# Revit family: 540_Sliding_Window_XXXX_Standard
name_source: partatom
category: Windows
revit_build: Autodesk Revit 2014 (Build: 20130308_1515(x64)
units: mm (PartAtom-declared; Revit-internal decimal feet)

## types (81) — shared parameters
Astragal Sash Gap = 1 mm  [stored 0.00328084 ft]
Centered In Wall = Yes
Custom Sash Width Side = 1000 mm  [stored 3.28084 ft]
Default Sill Height = 800 mm
Description = Sliding window, XXXX
Equal Sash Width = Yes
Frame Thickness = 54 mm  [stored 0.177165 ft]
Heavy Duty Handle Gap = 27 mm
Limit Sash Height Max = 1500 mm  [stored 4.92126 ft]
Limit Sash Height Min = 300 mm  [stored 0.984252 ft]
Limit Sash Width Max = 1200 mm
Limit Sash Width Min = 300 mm  [stored 0.984252 ft]
Limit Window Height Max = 1580 mm
Limit Window Height Min = 380 mm
Limit Window Width Max = 4760 mm
Limit Window Width Min = 1160 mm
Manufacturer = Crealco
Model = 540
Sash Frame Seal = 3 mm  [stored 0.00984252 ft]
URL = http://www.crealco.co.za
Wall Closure = By host
zero-valued in all types: Custom Frame Offset From Exterior

## per-type parameters (varying)
- 540SW-1206XXXX-1000Pa: Area Middle Sash Glazing=0.08 m²; Area Side Sash Glazing=0.08 m²; Clearvue SHGC Value=0.379; Custom Windload=1000 mm  [stored 3.28084 ft]; Custom Window Height=590 mm  [stored 1.9357 ft]; Custom Window Width=1190 mm  [stored 3.9042 ft]; Energy Advantage SHGC Value=0.344; Energy Advantage U Value=6.73; Heavy Duty Handle=No; Heavy Duty Interlocker=No; Height=590 mm  [stored 1.9357 ft]; Intruderprufe LowE SHGC Value=0.322; Intruderprufe LowE U Value=6.61; Intruderprufe SHGC Value=0.359; Intruderprufe U Value=7.44; Is Heavy Duty Handle=0 mm  [stored 0 ft]; Is Heavy Duty Mullion=0 mm  [stored 0 ft]; Limit Sash Width Side Max=315 mm; Limit Sash Width Side Min=300 mm  [stored 0.984252 ft]; Max Pane Area=0.08 m²; Sash Height=510 mm; Sash Width Middle=308 mm; Sash Width Sides=308 mm; Standard Interlocker=Yes; Width=1190 mm  [stored 3.9042 ft]; Windload Design=1000 mm  [stored 3.28084 ft]
- 540SW-1506XXXX-1000Pa: Area Middle Sash Glazing=0.11 m²; Area Side Sash Glazing=0.11 m²; Clearvue SHGC Value=0.415; Custom Windload=1000 mm  [stored 3.28084 ft]; Custom Window Height=590 mm  [stored 1.9357 ft]; Custom Window Width=1490 mm  [stored 4.88845 ft]; Energy Advantage SHGC Value=0.376; Energy Advantage U Value=6.42; Heavy Duty Handle=No; Heavy Duty Interlocker=No; Height=590 mm  [stored 1.9357 ft]; Intruderprufe LowE SHGC Value=0.352; Intruderprufe LowE U Value=6.31; Intruderprufe SHGC Value=0.393; Intruderprufe U Value=7.24; Is Heavy Duty Handle=0 mm  [stored 0 ft]; Is Heavy Duty Mullion=0 mm  [stored 0 ft]; Limit Sash Width Side Max=465 mm; Limit Sash Width Side Min=300 mm  [stored 0.984252 ft]; Max Pane Area=0.11 m²; Sash Height=510 mm; Sash Width Middle=383 mm; Sash Width Sides=383 mm; Standard Interlocker=Yes; Width=1490 mm  [stored 4.88845 ft]; Windload Design=1000 mm  [stored 3.28084 ft]
- 540SW-2106XXXX-1000Pa: Area Middle Sash Glazing=0.17 m²; Area Side Sash Glazing=0.17 m²; Clearvue SHGC Value=0.457; Custom Windload=1000 mm  [stored 3.28084 ft]; Custom Window Height=590 mm  [stored 1.9357 ft]; Custom Window Width=2090 mm  [stored 6.85696 ft]; Energy Advantage SHGC Value=0.413; Energy Advantage U Value=6.07; Heavy Duty Handle=No; Heavy Duty Interlocker=No; Height=590 mm  [stored 1.9357 ft]; Intruderprufe LowE SHGC Value=0.386; Intruderprufe LowE U Value=5.96; Intruderprufe SHGC Value=0.432; Intruderprufe U Value=7.07; Is Heavy Duty Handle=0 mm  [stored 0 ft]; Is Heavy Duty Mullion=0 mm  [stored 0 ft]; Limit Sash Width Side Max=765 mm; Limit Sash Width Side Min=300 mm  [stored 0.984252 ft]; Max Pane Area=0.17 m²; Sash Height=510 mm; Sash Width Middle=533 mm; Sash Width Sides=533 mm; Standard Interlocker=Yes; Width=2090 mm  [stored 6.85696 ft]; Windload Design=1000 mm  [stored 3.28084 ft]
- 540SW-2406XXXX-1000Pa: Area Middle Sash Glazing=0.2 m²; Area Side Sash Glazing=0.2 m²; Clearvue SHGC Value=0.47; Custom Windload=1000 mm  [stored 3.28084 ft]; Custom Window Height=590 mm  [stored 1.9357 ft]; Custom Window Width=2390 mm  [stored 7.84121 ft]; Energy Advantage SHGC Value=0.424; Energy Advantage U Value=5.96; Heavy Duty Handle=No; Heavy Duty Interlocker=No; Height=590 mm  [stored 1.9357 ft]; Intruderprufe LowE SHGC Value=0.397; Intruderprufe LowE U Value=5.86; Intruderprufe SHGC Value=0.444; Intruderprufe U Value=6.94; Is Heavy Duty Handle=0 mm  [stored 0 ft]; Is Heavy Duty Mullion=0 mm  [stored 0 ft]; Limit Sash Width Side Max=915 mm; Limit Sash Width Side Min=300 mm  [stored 0.984252 ft]; Max Pane Area=0.2 m²; Sash Height=510 mm; Sash Width Middle=608 mm; Sash Width Sides=608 mm; Standard Interlocker=Yes; Width=2390 mm  [stored 7.84121 ft]; Windload Design=1000 mm  [stored 3.28084 ft]
- 540SW-2706XXXX-1000Pa: Area Middle Sash Glazing=0.23 m²; Area Side Sash Glazing=0.23 m²; Clearvue SHGC Value=0.48; Custom Windload=1000 mm  [stored 3.28084 ft]; Custom Window Height=590 mm  [stored 1.9357 ft]; Custom Window Width=2690 mm; Energy Advantage SHGC Value=0.433; Energy Advantage U Value=5.87; Heavy Duty Handle=No; Heavy Duty Interlocker=No; Height=590 mm  [stored 1.9357 ft]; Intruderprufe LowE SHGC Value=0.405; Intruderprufe LowE U Value=5.77; Intruderprufe SHGC Value=0.454; Intruderprufe U Value=6.89; Is Heavy Duty Handle=0 mm  [stored 0 ft]; Is Heavy Duty Mullion=0 mm  [stored 0 ft]; Limit Sash Width Side Max=1065 mm; Limit Sash Width Side Min=300 mm  [stored 0.984252 ft]; Max Pane Area=0.23 m²; Sash Height=510 mm; Sash Width Middle=683 mm; Sash Width Sides=683 mm; Standard Interlocker=Yes; Width=2690 mm; Windload Design=1000 mm  [stored 3.28084 ft]
- 540SW-3006XXXX-1000Pa: Area Middle Sash Glazing=0.26 m²; Area Side Sash Glazing=0.26 m²; Clearvue SHGC Value=0.488; Custom Windload=1000 mm  [stored 3.28084 ft]; Custom Window Height=590 mm  [stored 1.9357 ft]; Custom Window Width=2990 mm  [stored 9.80971 ft]; Energy Advantage SHGC Value=0.44; Energy Advantage U Value=5.8; Heavy Duty Handle=No; Heavy Duty Interlocker=No; Height=590 mm  [stored 1.9357 ft]; Intruderprufe LowE SHGC Value=0.411; Intruderprufe LowE U Value=5.71; Intruderprufe SHGC Value=0.461; Intruderprufe U Value=6.84; Is Heavy Duty Handle=0 mm  [stored 0 ft]; Is Heavy Duty Mullion=0 mm  [stored 0 ft]; Limit Sash Width Side Max=1200 mm; Limit Sash Width Side Min=315 mm; Max Pane Area=0.26 m²; Sash Height=510 mm; Sash Width Middle=758 mm; Sash Width Sides=758 mm; Standard Interlocker=Yes; Width=2990 mm  [stored 9.80971 ft]; Windload Design=1000 mm  [stored 3.28084 ft]
- 540SW-1209XXXX-1000Pa: Area Middle Sash Glazing=0.14 m²; Area Side Sash Glazing=0.14 m²; Clearvue SHGC Value=0.44; Custom Windload=1000 mm  [stored 3.28084 ft]; Custom Window Height=890 mm  [stored 2.91995 ft]; Custom Window Width=1190 mm  [stored 3.9042 ft]; Energy Advantage SHGC Value=0.399; Energy Advantage U Value=6.54; Heavy Duty Handle=No; Heavy Duty Interlocker=No; Height=890 mm  [stored 2.91995 ft]; Intruderprufe LowE SHGC Value=0.373; Intruderprufe LowE U Value=6.43; Intruderprufe SHGC Value=0.417; Intruderprufe U Value=7.42; Is Heavy Duty Handle=0 mm  [stored 0 ft]; Is Heavy Duty Mullion=0 mm  [stored 0 ft]; Limit Sash Width Side Max=315 mm; Limit Sash Width Side Min=300 mm  [stored 0.984252 ft]; Max Pane Area=0.14 m²; Sash Height=810 mm; Sash Width Middle=308 mm; Sash Width Sides=308 mm; Standard Interlocker=Yes; Width=1190 mm  [stored 3.9042 ft]; Windload Design=1000 mm  [stored 3.28084 ft]
- 540SW-1509XXXX-1000Pa: Area Middle Sash Glazing=0.19 m²; Area Side Sash Glazing=0.19 m²; Clearvue SHGC Value=0.484; Custom Windload=1000 mm  [stored 3.28084 ft]; Custom Window Height=890 mm  [stored 2.91995 ft]; Custom Window Width=1490 mm  [stored 4.88845 ft]; Energy Advantage SHGC Value=0.438; Energy Advantage U Value=6.17; Heavy Duty Handle=No; Heavy Duty Interlocker=No; Height=890 mm  [stored 2.91995 ft]; Intruderprufe LowE SHGC Value=0.408; Intruderprufe LowE U Value=6.06; Intruderprufe SHGC Value=0.458; Intruderprufe U Value=7.18; Is Heavy Duty Handle=0 mm  [stored 0 ft]; Is Heavy Duty Mullion=0 mm  [stored 0 ft]; Limit Sash Width Side Max=465 mm; Limit Sash Width Side Min=300 mm  [stored 0.984252 ft]; Max Pane Area=0.19 m²; Sash Height=810 mm; Sash Width Middle=383 mm; Sash Width Sides=383 mm; Standard Interlocker=Yes; Width=1490 mm  [stored 4.88845 ft]; Windload Design=1000 mm  [stored 3.28084 ft]
- 540SW-1809XXXX-1000Pa: Area Middle Sash Glazing=0.25 m²; Area Side Sash Glazing=0.25 m²; Clearvue SHGC Value=0.513; Custom Windload=1000 mm  [stored 3.28084 ft]; Custom Window Height=890 mm  [stored 2.91995 ft]; Custom Window Width=1790 mm  [stored 5.8727 ft]; Energy Advantage SHGC Value=0.463; Energy Advantage U Value=5.92; Heavy Duty Handle=No; Heavy Duty Interlocker=No; Height=890 mm  [stored 2.91995 ft]; Intruderprufe LowE SHGC Value=0.432; Intruderprufe LowE U Value=5.82; Intruderprufe SHGC Value=0.485; Intruderprufe U Value=7.02; Is Heavy Duty Handle=0 mm  [stored 0 ft]; Is Heavy Duty Mullion=0 mm  [stored 0 ft]; Limit Sash Width Side Max=615 mm; Limit Sash Width Side Min=300 mm  [stored 0.984252 ft]; Max Pane Area=0.25 m²; Sash Height=810 mm; Sash Width Middle=458 mm; Sash Width Sides=458 mm; Standard Interlocker=Yes; Width=1790 mm  [stored 5.8727 ft]; Windload Design=1000 mm  [stored 3.28084 ft]
- 540SW-2109XXXX-1000Pa: Area Middle Sash Glazing=0.3 m²; Area Side Sash Glazing=0.3 m²; Clearvue SHGC Value=0.534; Custom Windload=1000 mm  [stored 3.28084 ft]; Custom Window Height=890 mm  [stored 2.91995 ft]; Custom Window Width=2090 mm  [stored 6.85696 ft]; Energy Advantage SHGC Value=0.481; Energy Advantage U Value=5.75; Heavy Duty Handle=No; Heavy Duty Interlocker=No; Height=890 mm  [stored 2.91995 ft]; Intruderprufe LowE SHGC Value=0.449; Intruderprufe LowE U Value=5.64; Intruderprufe SHGC Value=0.504; Intruderprufe U Value=6.9; Is Heavy Duty Handle=0 mm  [stored 0 ft]; Is Heavy Duty Mullion=0 mm  [stored 0 ft]; Limit Sash Width Side Max=765 mm; Limit Sash Width Side Min=300 mm  [stored 0.984252 ft]; Max Pane Area=0.3 m²; Sash Height=810 mm; Sash Width Middle=533 mm; Sash Width Sides=533 mm; Standard Interlocker=Yes; Width=2090 mm  [stored 6.85696 ft]; Windload Design=1000 mm  [stored 3.28084 ft]
- 540SW-2409XXXX-1000Pa: Area Middle Sash Glazing=0.35 m²; Area Side Sash Glazing=0.35 m²; Clearvue SHGC Value=0.55; Custom Windload=1000 mm  [stored 3.28084 ft]; Custom Window Height=890 mm  [stored 2.91995 ft]; Custom Window Width=2390 mm  [stored 7.84121 ft]; Energy Advantage SHGC Value=0.495; Energy Advantage U Value=5.61; Heavy Duty Handle=No; Heavy Duty Interlocker=No; Height=890 mm  [stored 2.91995 ft]; Intruderprufe LowE SHGC Value=0.461; Intruderprufe LowE U Value=5.51; Intruderprufe SHGC Value=0.519; Intruderprufe U Value=6.82; Is Heavy Duty Handle=0 mm  [stored 0 ft]; Is Heavy Duty Mullion=0 mm  [stored 0 ft]; Limit Sash Width Side Max=915 mm; Limit Sash Width Side Min=300 mm  [stored 0.984252 ft]; Max Pane Area=0.35 m²; Sash Height=810 mm; Sash Width Middle=608 mm; Sash Width Sides=608 mm; Standard Interlocker=Yes; Width=2390 mm  [stored 7.84121 ft]; Windload Design=1000 mm  [stored 3.28084 ft]
- 540SW-2709XXXX-1000Pa: Area Middle Sash Glazing=0.4 m²; Area Side Sash Glazing=0.4 m²; Clearvue SHGC Value=0.562; Custom Windload=1000 mm  [stored 3.28084 ft]; Custom Window Height=890 mm  [stored 2.91995 ft]; Custom Window Width=2690 mm; Energy Advantage SHGC Value=0.505; Energy Advantage U Value=5.51; Heavy Duty Handle=No; Heavy Duty Interlocker=No; Height=890 mm  [stored 2.91995 ft]; Intruderprufe LowE SHGC Value=0.471; Intruderprufe LowE U Value=5.41; Intruderprufe SHGC Value=0.53; Intruderprufe U Value=6.75; Is Heavy Duty Handle=0 mm  [stored 0 ft]; Is Heavy Duty Mullion=0 mm  [stored 0 ft]; Limit Sash Width Side Max=1065 mm; Limit Sash Width Side Min=300 mm  [stored 0.984252 ft]; Max Pane Area=0.4 m²; Sash Height=810 mm; Sash Width Middle=683 mm; Sash Width Sides=683 mm; Standard Interlocker=Yes; Width=2690 mm; Windload Design=1000 mm  [stored 3.28084 ft]
- 540SW-3009XXXX-1000Pa: Area Middle Sash Glazing=0.46 m²; Area Side Sash Glazing=0.46 m²; Clearvue SHGC Value=0.572; Custom Windload=1000 mm  [stored 3.28084 ft]; Custom Window Height=890 mm  [stored 2.91995 ft]; Custom Window Width=2990 mm  [stored 9.80971 ft]; Energy Advantage SHGC Value=0.514; Energy Advantage U Value=5.43; Heavy Duty Handle=No; Heavy Duty Interlocker=No; Height=890 mm  [stored 2.91995 ft]; Intruderprufe LowE SHGC Value=0.479; Intruderprufe LowE U Value=5.33; Intruderprufe SHGC Value=0.539; Intruderprufe U Value=6.7; Is Heavy Duty Handle=0 mm  [stored 0 ft]; Is Heavy Duty Mullion=0 mm  [stored 0 ft]; Limit Sash Width Side Max=1200 mm; Limit Sash Width Side Min=315 mm; Max Pane Area=0.46 m²; Sash Height=810 mm; Sash Width Middle=758 mm; Sash Width Sides=758 mm; Standard Interlocker=Yes; Width=2990 mm  [stored 9.80971 ft]; Windload Design=1000 mm  [stored 3.28084 ft]
- 540SW-1212XXXX-1000Pa: Area Middle Sash Glazing=0.2 m²; Area Side Sash Glazing=0.2 m²; Clearvue SHGC Value=0.471; Custom Windload=1000 mm  [stored 3.28084 ft]; Custom Window Height=1190 mm  [stored 3.9042 ft]; Custom Window Width=1190 mm  [stored 3.9042 ft]; Energy Advantage SHGC Value=0.426; Energy Advantage U Value=6.45; Heavy Duty Handle=No; Heavy Duty Interlocker=No; Height=1190 mm  [stored 3.9042 ft]; Intruderprufe LowE SHGC Value=0.398; Intruderprufe LowE U Value=6.34; Intruderprufe SHGC Value=0.445; Intruderprufe U Value=7.41; Is Heavy Duty Handle=0 mm  [stored 0 ft]; Is Heavy Duty Mullion=0 mm  [stored 0 ft]; Limit Sash Width Side Max=315 mm; Limit Sash Width Side Min=300 mm  [stored 0.984252 ft]; Max Pane Area=0.2 m²; Sash Height=1110 mm; Sash Width Middle=308 mm; Sash Width Sides=308 mm; Standard Interlocker=Yes; Width=1190 mm  [stored 3.9042 ft]; Windload Design=1000 mm  [stored 3.28084 ft]
- 540SW-1512XXXX-1000Pa: Area Middle Sash Glazing=0.28 m²; Area Side Sash Glazing=0.28 m²; Clearvue SHGC Value=0.518; Custom Windload=1000 mm  [stored 3.28084 ft]; Custom Window Height=1190 mm  [stored 3.9042 ft]; Custom Window Width=1490 mm  [stored 4.88845 ft]; Energy Advantage SHGC Value=0.468; Energy Advantage U Value=6.05; Heavy Duty Handle=No; Heavy Duty Interlocker=No; Height=1190 mm  [stored 3.9042 ft]; Intruderprufe LowE SHGC Value=0.436; Intruderprufe LowE U Value=5.94; Intruderprufe SHGC Value=0.49; Intruderprufe U Value=7.15; Is Heavy Duty Handle=0 mm  [stored 0 ft]; Is Heavy Duty Mullion=0 mm  [stored 0 ft]; Limit Sash Width Side Max=465 mm; Limit Sash Width Side Min=300 mm  [stored 0.984252 ft]; Max Pane Area=0.28 m²; Sash Height=1110 mm; Sash Width Middle=383 mm; Sash Width Sides=383 mm; Standard Interlocker=Yes; Width=1490 mm  [stored 4.88845 ft]; Windload Design=1000 mm  [stored 3.28084 ft]
- 540SW-1812XXXX-1000Pa: Area Middle Sash Glazing=0.35 m²; Area Side Sash Glazing=0.35 m²; Clearvue SHGC Value=0.55; Custom Windload=1000 mm  [stored 3.28084 ft]; Custom Window Height=1190 mm  [stored 3.9042 ft]; Custom Window Width=1790 mm  [stored 5.8727 ft]; Energy Advantage SHGC Value=0.495; Energy Advantage U Value=5.78; Heavy Duty Handle=No; Heavy Duty Interlocker=No; Height=1190 mm  [stored 3.9042 ft]; Intruderprufe LowE SHGC Value=0.462; Intruderprufe LowE U Value=5.68; Intruderprufe SHGC Value=0.519; Intruderprufe U Value=6.97; Is Heavy Duty Handle=0 mm  [stored 0 ft]; Is Heavy Duty Mullion=0 mm  [stored 0 ft]; Limit Sash Width Side Max=615 mm; Limit Sash Width Side Min=300 mm  [stored 0.984252 ft]; Max Pane Area=0.35 m²; Sash Height=1110 mm; Sash Width Middle=458 mm; Sash Width Sides=458 mm; Standard Interlocker=Yes; Width=1790 mm  [stored 5.8727 ft]; Windload Design=1000 mm  [stored 3.28084 ft]
- 540SW-2112XXXX-1000Pa: Area Middle Sash Glazing=0.43 m²; Area Side Sash Glazing=0.43 m²; Clearvue SHGC Value=0.572; Custom Windload=1000 mm  [stored 3.28084 ft]; Custom Window Height=1190 mm  [stored 3.9042 ft]; Custom Window Width=2090 mm  [stored 6.85696 ft]; Energy Advantage SHGC Value=0.515; Energy Advantage U Value=5.59; Heavy Duty Handle=No; Heavy Duty Interlocker=No; Height=1190 mm  [stored 3.9042 ft]; Intruderprufe LowE SHGC Value=0.48; Intruderprufe LowE U Value=4.59; Intruderprufe SHGC Value=0.54; Intruderprufe U Value=6.85; Is Heavy Duty Handle=0 mm  [stored 0 ft]; Is Heavy Duty Mullion=0 mm  [stored 0 ft]; Limit Sash Width Side Max=765 mm; Limit Sash Width Side Min=300 mm  [stored 0.984252 ft]; Max Pane Area=0.43 m²; Sash Height=1110 mm; Sash Width Middle=533 mm; Sash Width Sides=533 mm; Standard Interlocker=Yes; Width=2090 mm  [stored 6.85696 ft]; Windload Design=1000 mm  [stored 3.28084 ft]
- 540SW-2412XXXX-1000Pa: Area Middle Sash Glazing=0.5 m²; Area Side Sash Glazing=0.5 m²; Clearvue SHGC Value=0.589; Custom Windload=1000 mm  [stored 3.28084 ft]; Custom Window Height=1190 mm  [stored 3.9042 ft]; Custom Window Width=2390 mm  [stored 7.84121 ft]; Energy Advantage SHGC Value=0.53; Energy Advantage U Value=5.44; Heavy Duty Handle=No; Heavy Duty Interlocker=No; Height=1190 mm  [stored 3.9042 ft]; Intruderprufe LowE SHGC Value=0.494; Intruderprufe LowE U Value=5.35; Intruderprufe SHGC Value=0.556; Intruderprufe U Value=6.75; Is Heavy Duty Handle=0 mm  [stored 0 ft]; Is Heavy Duty Mullion=0 mm  [stored 0 ft]; Limit Sash Width Side Max=915 mm; Limit Sash Width Side Min=300 mm  [stored 0.984252 ft]; Max Pane Area=0.5 m²; Sash Height=1110 mm; Sash Width Middle=608 mm; Sash Width Sides=608 mm; Standard Interlocker=Yes; Width=2390 mm  [stored 7.84121 ft]; Windload Design=1000 mm  [stored 3.28084 ft]
- 540SW-2712XXXX-1000Pa: Area Middle Sash Glazing=0.58 m²; Area Side Sash Glazing=0.58 m²; Clearvue SHGC Value=0.602; Custom Windload=1000 mm  [stored 3.28084 ft]; Custom Window Height=1190 mm  [stored 3.9042 ft]; Custom Window Width=2690 mm; Energy Advantage SHGC Value=0.541; Energy Advantage U Value=5.33; Heavy Duty Handle=No; Heavy Duty Interlocker=No; Height=1190 mm  [stored 3.9042 ft]; Intruderprufe LowE SHGC Value=0.504; Intruderprufe LowE U Value=5.24; Intruderprufe SHGC Value=0.568; Intruderprufe U Value=6.68; Is Heavy Duty Handle=0 mm  [stored 0 ft]; Is Heavy Duty Mullion=0 mm  [stored 0 ft]; Limit Sash Width Side Max=1065 mm; Limit Sash Width Side Min=300 mm  [stored 0.984252 ft]; Max Pane Area=0.58 m²; Sash Height=1110 mm; Sash Width Middle=683 mm; Sash Width Sides=683 mm; Standard Interlocker=Yes; Width=2690 mm; Windload Design=1000 mm  [stored 3.28084 ft]
- 540SW-3012XXXX-1000Pa: Area Middle Sash Glazing=0.65 m²; Area Side Sash Glazing=0.65 m²; Clearvue SHGC Value=0.613; Custom Windload=1000 mm  [stored 3.28084 ft]; Custom Window Height=1190 mm  [stored 3.9042 ft]; Custom Window Width=2990 mm  [stored 9.80971 ft]; Energy Advantage SHGC Value=0.55; Energy Advantage U Value=5.24; Heavy Duty Handle=No; Heavy Duty Interlocker=No; Height=1190 mm  [stored 3.9042 ft]; Intruderprufe LowE SHGC Value=0.513; Intruderprufe LowE U Value=5.15; Intruderprufe SHGC Value=0.578; Intruderprufe U Value=6.62; Is Heavy Duty Handle=0 mm  [stored 0 ft]; Is Heavy Duty Mullion=0 mm  [stored 0 ft]; Limit Sash Width Side Max=1200 mm; Limit Sash Width Side Min=315 mm; Max Pane Area=0.65 m²; Sash Height=1110 mm; Sash Width Middle=758 mm; Sash Width Sides=758 mm; Standard Interlocker=Yes; Width=2990 mm  [stored 9.80971 ft]; Windload Design=1000 mm  [stored 3.28084 ft]
- 540SW-1215XXXX-1000Pa: Area Middle Sash Glazing=0.26 m²; Area Side Sash Glazing=0.26 m²; Clearvue SHGC Value=0.489; Custom Windload=1000 mm  [stored 3.28084 ft]; Custom Window Height=1490 mm  [stored 4.88845 ft]; Custom Window Width=1190 mm  [stored 3.9042 ft]; Energy Advantage SHGC Value=0.443; Energy Advantage U Value=6.39; Heavy Duty Handle=No; Heavy Duty Interlocker=No; Height=1490 mm  [stored 4.88845 ft]; Intruderprufe LowE SHGC Value=0.413; Intruderprufe LowE U Value=6.28; Intruderprufe SHGC Value=0.463; Intruderprufe U Value=7.41; Is Heavy Duty Handle=0 mm  [stored 0 ft]; Is Heavy Duty Mullion=0 mm  [stored 0 ft]; Limit Sash Width Side Max=315 mm; Limit Sash Width Side Min=300 mm  [stored 0.984252 ft]; Max Pane Area=0.26 m²; Sash Height=1410 mm; Sash Width Middle=308 mm; Sash Width Sides=308 mm; Standard Interlocker=Yes; Width=1190 mm  [stored 3.9042 ft]; Windload Design=1000 mm  [stored 3.28084 ft]
- 540SW-1515XXXX-1000Pa: Area Middle Sash Glazing=0.36 m²; Area Side Sash Glazing=0.36 m²; Clearvue SHGC Value=0.539; Custom Windload=1000 mm  [stored 3.28084 ft]; Custom Window Height=1490 mm  [stored 4.88845 ft]; Custom Window Width=1490 mm  [stored 4.88845 ft]; Energy Advantage SHGC Value=0.486; Energy Advantage U Value=5.97; Heavy Duty Handle=No; Heavy Duty Interlocker=No; Height=1490 mm  [stored 4.88845 ft]; Intruderprufe LowE SHGC Value=0.453; Intruderprufe LowE U Value=5.87; Intruderprufe SHGC Value=0.509; Intruderprufe U Value=7.13; Is Heavy Duty Handle=0 mm  [stored 0 ft]; Is Heavy Duty Mullion=0 mm  [stored 0 ft]; Limit Sash Width Side Max=465 mm; Limit Sash Width Side Min=300 mm  [stored 0.984252 ft]; Max Pane Area=0.36 m²; Sash Height=1410 mm; Sash Width Middle=383 mm; Sash Width Sides=383 mm; Standard Interlocker=Yes; Width=1490 mm  [stored 4.88845 ft]; Windload Design=1000 mm  [stored 3.28084 ft]
- 540SW-1815XXXX-1000Pa: Area Middle Sash Glazing=0.46 m²; Area Side Sash Glazing=0.46 m²; Clearvue SHGC Value=0.572; Custom Windload=1000 mm  [stored 3.28084 ft]; Custom Window Height=1490 mm  [stored 4.88845 ft]; Custom Window Width=1790 mm  [stored 5.8727 ft]; Energy Advantage SHGC Value=0.515; Energy Advantage U Value=5.69; Heavy Duty Handle=No; Heavy Duty Interlocker=No; Height=1490 mm  [stored 4.88845 ft]; Intruderprufe LowE SHGC Value=0.479; Intruderprufe LowE U Value=5.59; Intruderprufe SHGC Value=0.54; Intruderprufe U Value=6.94; Is Heavy Duty Handle=0 mm  [stored 0 ft]; Is Heavy Duty Mullion=0 mm  [stored 0 ft]; Limit Sash Width Side Max=615 mm; Limit Sash Width Side Min=300 mm  [stored 0.984252 ft]; Max Pane Area=0.46 m²; Sash Height=1410 mm; Sash Width Middle=458 mm; Sash Width Sides=458 mm; Standard Interlocker=Yes; Width=1790 mm  [stored 5.8727 ft]; Windload Design=1000 mm  [stored 3.28084 ft]
- 540SW-2115XXXX-1000Pa: Area Middle Sash Glazing=0.55 m²; Area Side Sash Glazing=0.55 m²; Clearvue SHGC Value=0.595; Custom Windload=1000 mm  [stored 3.28084 ft]; Custom Window Height=1490 mm  [stored 4.88845 ft]; Custom Window Width=2090 mm  [stored 6.85696 ft]; Energy Advantage SHGC Value=0.535; Energy Advantage U Value=5.49; Heavy Duty Handle=No; Heavy Duty Interlocker=No; Height=1490 mm  [stored 4.88845 ft]; Intruderprufe LowE SHGC Value=0.498; Intruderprufe LowE U Value=5.39; Intruderprufe SHGC Value=0.562; Intruderprufe U Value=6.81; Is Heavy Duty Handle=0 mm  [stored 0 ft]; Is Heavy Duty Mullion=0 mm  [stored 0 ft]; Limit Sash Width Side Max=765 mm; Limit Sash Width Side Min=300 mm  [stored 0.984252 ft]; Max Pane Area=0.55 m²; Sash Height=1410 mm; Sash Width Middle=533 mm; Sash Width Sides=533 mm; Standard Interlocker=Yes; Width=2090 mm  [stored 6.85696 ft]; Windload Design=1000 mm  [stored 3.28084 ft]
- 540SW-2415XXXX-1000Pa: Area Middle Sash Glazing=0.65 m²; Area Side Sash Glazing=0.65 m²; Clearvue SHGC Value=0.613; Custom Windload=1000 mm  [stored 3.28084 ft]; Custom Window Height=1490 mm  [stored 4.88845 ft]; Custom Window Width=2390 mm  [stored 7.84121 ft]; Energy Advantage SHGC Value=0.551; Energy Advantage U Value=5.34; Heavy Duty Handle=No; Heavy Duty Interlocker=No; Height=1490 mm  [stored 4.88845 ft]; Intruderprufe LowE SHGC Value=0.513; Intruderprufe LowE U Value=5.24; Intruderprufe SHGC Value=0.578; Intruderprufe U Value=6.72; Is Heavy Duty Handle=0 mm  [stored 0 ft]; Is Heavy Duty Mullion=0 mm  [stored 0 ft]; Limit Sash Width Side Max=915 mm; Limit Sash Width Side Min=300 mm  [stored 0.984252 ft]; Max Pane Area=0.65 m²; Sash Height=1410 mm; Sash Width Middle=608 mm; Sash Width Sides=608 mm; Standard Interlocker=Yes; Width=2390 mm  [stored 7.84121 ft]; Windload Design=1000 mm  [stored 3.28084 ft]
- 540SW-2715XXXX-1000Pa: Area Middle Sash Glazing=0.75 m²; Area Side Sash Glazing=0.75 m²; Clearvue SHGC Value=0.627; Custom Windload=1000 mm  [stored 3.28084 ft]; Custom Window Height=1490 mm  [stored 4.88845 ft]; Custom Window Width=2690 mm; Energy Advantage SHGC Value=0.563; Energy Advantage U Value=5.22; Heavy Duty Handle=No; Heavy Duty Interlocker=No; Height=1490 mm  [stored 4.88845 ft]; Intruderprufe LowE SHGC Value=0.524; Intruderprufe LowE U Value=5.13; Intruderprufe SHGC Value=0.591; Intruderprufe U Value=6.64; Is Heavy Duty Handle=0 mm  [stored 0 ft]; Is Heavy Duty Mullion=0 mm  [stored 0 ft]; Limit Sash Width Side Max=1065 mm; Limit Sash Width Side Min=300 mm  [stored 0.984252 ft]; Max Pane Area=0.75 m²; Sash Height=1410 mm; Sash Width Middle=683 mm; Sash Width Sides=683 mm; Standard Interlocker=Yes; Width=2690 mm; Windload Design=1000 mm  [stored 3.28084 ft]
- 540SW-3015XXXX-1000Pa: Area Middle Sash Glazing=0.85 m²; Area Side Sash Glazing=0.85 m²; Clearvue SHGC Value=0.637; Custom Windload=1000 mm  [stored 3.28084 ft]; Custom Window Height=1490 mm  [stored 4.88845 ft]; Custom Window Width=2990 mm  [stored 9.80971 ft]; Energy Advantage SHGC Value=0.572; Energy Advantage U Value=5.13; Heavy Duty Handle=Yes; Heavy Duty Interlocker=Yes; Height=1490 mm  [stored 4.88845 ft]; Intruderprufe LowE SHGC Value=0.533; Intruderprufe LowE U Value=5.04; Intruderprufe SHGC Value=0.601; Intruderprufe U Value=6.58; Is Heavy Duty Handle=1 mm  [stored 0.00328084 ft]; Is Heavy Duty Mullion=1 mm  [stored 0.00328084 ft]; Limit Sash Width Side Max=1200 mm; Limit Sash Width Side Min=315 mm; Max Pane Area=0.85 m²; Sash Height=1410 mm; Sash Width Middle=758 mm; Sash Width Sides=758 mm; Standard Interlocker=No; Width=2990 mm  [stored 9.80971 ft]; Windload Design=1000 mm  [stored 3.28084 ft]
- 540SW-1206XXXX-1500Pa: Area Middle Sash Glazing=0.08 m²; Area Side Sash Glazing=0.08 m²; Clearvue SHGC Value=0.379; Custom Windload=1500 mm  [stored 4.92126 ft]; Custom Window Height=590 mm  [stored 1.9357 ft]; Custom Window Width=1190 mm  [stored 3.9042 ft]; Energy Advantage SHGC Value=0.344; Energy Advantage U Value=6.73; Heavy Duty Handle=No; Heavy Duty Interlocker=No; Height=590 mm  [stored 1.9357 ft]; Intruderprufe LowE SHGC Value=0.322; Intruderprufe LowE U Value=6.61; Intruderprufe SHGC Value=0.359; Intruderprufe U Value=7.44; Is Heavy Duty Handle=0 mm  [stored 0 ft]; Is Heavy Duty Mullion=0 mm  [stored 0 ft]; Limit Sash Width Side Max=315 mm; Limit Sash Width Side Min=300 mm  [stored 0.984252 ft]; Max Pane Area=0.08 m²; Sash Height=510 mm; Sash Width Middle=308 mm; Sash Width Sides=308 mm; Standard Interlocker=Yes; Width=1190 mm  [stored 3.9042 ft]; Windload Design=1500 mm  [stored 4.92126 ft]
- 540SW-1206XXXX-2000Pa: Area Middle Sash Glazing=0.08 m²; Area Side Sash Glazing=0.08 m²; Clearvue SHGC Value=0.379; Custom Windload=2000 mm  [stored 6.56168 ft]; Custom Window Height=590 mm  [stored 1.9357 ft]; Custom Window Width=1190 mm  [stored 3.9042 ft]; Energy Advantage SHGC Value=0.344; Energy Advantage U Value=6.73; Heavy Duty Handle=No; Heavy Duty Interlocker=No; Height=590 mm  [stored 1.9357 ft]; Intruderprufe LowE SHGC Value=0.322; Intruderprufe LowE U Value=6.61; Intruderprufe SHGC Value=0.359; Intruderprufe U Value=7.44; Is Heavy Duty Handle=0 mm  [stored 0 ft]; Is Heavy Duty Mullion=0 mm  [stored 0 ft]; Limit Sash Width Side Max=315 mm; Limit Sash Width Side Min=300 mm  [stored 0.984252 ft]; Max Pane Area=0.08 m²; Sash Height=510 mm; Sash Width Middle=308 mm; Sash Width Sides=308 mm; Standard Interlocker=Yes; Width=1190 mm  [stored 3.9042 ft]; Windload Design=2000 mm  [stored 6.56168 ft]
- 540SW-1209XXXX-1500Pa: Area Middle Sash Glazing=0.14 m²; Area Side Sash Glazing=0.14 m²; Clearvue SHGC Value=0.44; Custom Windload=1500 mm  [stored 4.92126 ft]; Custom Window Height=890 mm  [stored 2.91995 ft]; Custom Window Width=1190 mm  [stored 3.9042 ft]; Energy Advantage SHGC Value=0.399; Energy Advantage U Value=6.54; Heavy Duty Handle=No; Heavy Duty Interlocker=No; Height=890 mm  [stored 2.91995 ft]; Intruderprufe LowE SHGC Value=0.373; Intruderprufe LowE U Value=6.43; Intruderprufe SHGC Value=0.417; Intruderprufe U Value=7.42; Is Heavy Duty Handle=0 mm  [stored 0 ft]; Is Heavy Duty Mullion=0 mm  [stored 0 ft]; Limit Sash Width Side Max=315 mm; Limit Sash Width Side Min=300 mm  [stored 0.984252 ft]; Max Pane Area=0.14 m²; Sash Height=810 mm; Sash Width Middle=308 mm; Sash Width Sides=308 mm; Standard Interlocker=Yes; Width=1190 mm  [stored 3.9042 ft]; Windload Design=1500 mm  [stored 4.92126 ft]
- 540SW-1209XXXX-2000Pa: Area Middle Sash Glazing=0.14 m²; Area Side Sash Glazing=0.14 m²; Clearvue SHGC Value=0.44; Custom Windload=2000 mm  [stored 6.56168 ft]; Custom Window Height=890 mm  [stored 2.91995 ft]; Custom Window Width=1190 mm  [stored 3.9042 ft]; Energy Advantage SHGC Value=0.399; Energy Advantage U Value=6.54; Heavy Duty Handle=No; Heavy Duty Interlocker=No; Height=890 mm  [stored 2.91995 ft]; Intruderprufe LowE SHGC Value=0.373; Intruderprufe LowE U Value=6.43; Intruderprufe SHGC Value=0.417; Intruderprufe U Value=7.42; Is Heavy Duty Handle=0 mm  [stored 0 ft]; Is Heavy Duty Mullion=0 mm  [stored 0 ft]; Limit Sash Width Side Max=315 mm; Limit Sash Width Side Min=300 mm  [stored 0.984252 ft]; Max Pane Area=0.14 m²; Sash Height=810 mm; Sash Width Middle=308 mm; Sash Width Sides=308 mm; Standard Interlocker=Yes; Width=1190 mm  [stored 3.9042 ft]; Windload Design=2000 mm  [stored 6.56168 ft]
- 540SW-1212XXXX-1500Pa: Area Middle Sash Glazing=0.2 m²; Area Side Sash Glazing=0.2 m²; Clearvue SHGC Value=0.471; Custom Windload=1500 mm  [stored 4.92126 ft]; Custom Window Height=1190 mm  [stored 3.9042 ft]; Custom Window Width=1190 mm  [stored 3.9042 ft]; Energy Advantage SHGC Value=0.426; Energy Advantage U Value=6.45; Heavy Duty Handle=No; Heavy Duty Interlocker=No; Height=1190 mm  [stored 3.9042 ft]; Intruderprufe LowE SHGC Value=0.398; Intruderprufe LowE U Value=6.34; Intruderprufe SHGC Value=0.445; Intruderprufe U Value=7.41; Is Heavy Duty Handle=0 mm  [stored 0 ft]; Is Heavy Duty Mullion=0 mm  [stored 0 ft]; Limit Sash Width Side Max=315 mm; Limit Sash Width Side Min=300 mm  [stored 0.984252 ft]; Max Pane Area=0.2 m²; Sash Height=1110 mm; Sash Width Middle=308 mm; Sash Width Sides=308 mm; Standard Interlocker=Yes; Width=1190 mm  [stored 3.9042 ft]; Windload Design=1500 mm  [stored 4.92126 ft]
- 540SW-1212XXXX-2000Pa: Area Middle Sash Glazing=0.2 m²; Area Side Sash Glazing=0.2 m²; Clearvue SHGC Value=0.471; Custom Windload=2000 mm  [stored 6.56168 ft]; Custom Window Height=1190 mm  [stored 3.9042 ft]; Custom Window Width=1190 mm  [stored 3.9042 ft]; Energy Advantage SHGC Value=0.426; Energy Advantage U Value=6.45; Heavy Duty Handle=No; Heavy Duty Interlocker=No; Height=1190 mm  [stored 3.9042 ft]; Intruderprufe LowE SHGC Value=0.398; Intruderprufe LowE U Value=6.34; Intruderprufe SHGC Value=0.445; Intruderprufe U Value=7.41; Is Heavy Duty Handle=0 mm  [stored 0 ft]; Is Heavy Duty Mullion=0 mm  [stored 0 ft]; Limit Sash Width Side Max=315 mm; Limit Sash Width Side Min=300 mm  [stored 0.984252 ft]; Max Pane Area=0.2 m²; Sash Height=1110 mm; Sash Width Middle=308 mm; Sash Width Sides=308 mm; Standard Interlocker=Yes; Width=1190 mm  [stored 3.9042 ft]; Windload Design=2000 mm  [stored 6.56168 ft]
- 540SW-1215XXXX-1500Pa: Area Middle Sash Glazing=0.26 m²; Area Side Sash Glazing=0.26 m²; Clearvue SHGC Value=0.489; Custom Windload=1500 mm  [stored 4.92126 ft]; Custom Window Height=1490 mm  [stored 4.88845 ft]; Custom Window Width=1190 mm  [stored 3.9042 ft]; Energy Advantage SHGC Value=0.443; Energy Advantage U Value=6.39; Heavy Duty Handle=No; Heavy Duty Interlocker=No; Height=1490 mm  [stored 4.88845 ft]; Intruderprufe LowE SHGC Value=0.413; Intruderprufe LowE U Value=6.28; Intruderprufe SHGC Value=0.463; Intruderprufe U Value=7.41; Is Heavy Duty Handle=0 mm  [stored 0 ft]; Is Heavy Duty Mullion=0 mm  [stored 0 ft]; Limit Sash Width Side Max=315 mm; Limit Sash Width Side Min=300 mm  [stored 0.984252 ft]; Max Pane Area=0.26 m²; Sash Height=1410 mm; Sash Width Middle=308 mm; Sash Width Sides=308 mm; Standard Interlocker=Yes; Width=1190 mm  [stored 3.9042 ft]; Windload Design=1500 mm  [stored 4.92126 ft]
- 540SW-1215XXXX-2000Pa: Area Middle Sash Glazing=0.26 m²; Area Side Sash Glazing=0.26 m²; Clearvue SHGC Value=0.489; Custom Windload=2000 mm  [stored 6.56168 ft]; Custom Window Height=1490 mm  [stored 4.88845 ft]; Custom Window Width=1190 mm  [stored 3.9042 ft]; Energy Advantage SHGC Value=0.443; Energy Advantage U Value=6.39; Heavy Duty Handle=No; Heavy Duty Interlocker=No; Height=1490 mm  [stored 4.88845 ft]; Intruderprufe LowE SHGC Value=0.413; Intruderprufe LowE U Value=6.28; Intruderprufe SHGC Value=0.463; Intruderprufe U Value=7.41; Is Heavy Duty Handle=0 mm  [stored 0 ft]; Is Heavy Duty Mullion=0 mm  [stored 0 ft]; Limit Sash Width Side Max=315 mm; Limit Sash Width Side Min=300 mm  [stored 0.984252 ft]; Max Pane Area=0.26 m²; Sash Height=1410 mm; Sash Width Middle=308 mm; Sash Width Sides=308 mm; Standard Interlocker=Yes; Width=1190 mm  [stored 3.9042 ft]; Windload Design=2000 mm  [stored 6.56168 ft]
- 540SW-1506XXXX-1500Pa: Area Middle Sash Glazing=0.11 m²; Area Side Sash Glazing=0.11 m²; Clearvue SHGC Value=0.415; Custom Windload=1500 mm  [stored 4.92126 ft]; Custom Window Height=590 mm  [stored 1.9357 ft]; Custom Window Width=1490 mm  [stored 4.88845 ft]; Energy Advantage SHGC Value=0.376; Energy Advantage U Value=6.42; Heavy Duty Handle=No; Heavy Duty Interlocker=No; Height=590 mm  [stored 1.9357 ft]; Intruderprufe LowE SHGC Value=0.352; Intruderprufe LowE U Value=6.31; Intruderprufe SHGC Value=0.393; Intruderprufe U Value=7.24; Is Heavy Duty Handle=0 mm  [stored 0 ft]; Is Heavy Duty Mullion=0 mm  [stored 0 ft]; Limit Sash Width Side Max=465 mm; Limit Sash Width Side Min=300 mm  [stored 0.984252 ft]; Max Pane Area=0.11 m²; Sash Height=510 mm; Sash Width Middle=383 mm; Sash Width Sides=383 mm; Standard Interlocker=Yes; Width=1490 mm  [stored 4.88845 ft]; Windload Design=1500 mm  [stored 4.92126 ft]
- 540SW-1506XXXX-2000Pa: Area Middle Sash Glazing=0.11 m²; Area Side Sash Glazing=0.11 m²; Clearvue SHGC Value=0.415; Custom Windload=2000 mm  [stored 6.56168 ft]; Custom Window Height=590 mm  [stored 1.9357 ft]; Custom Window Width=1490 mm  [stored 4.88845 ft]; Energy Advantage SHGC Value=0.376; Energy Advantage U Value=6.42; Heavy Duty Handle=No; Heavy Duty Interlocker=No; Height=590 mm  [stored 1.9357 ft]; Intruderprufe LowE SHGC Value=0.352; Intruderprufe LowE U Value=6.31; Intruderprufe SHGC Value=0.393; Intruderprufe U Value=7.24; Is Heavy Duty Handle=0 mm  [stored 0 ft]; Is Heavy Duty Mullion=0 mm  [stored 0 ft]; Limit Sash Width Side Max=465 mm; Limit Sash Width Side Min=300 mm  [stored 0.984252 ft]; Max Pane Area=0.11 m²; Sash Height=510 mm; Sash Width Middle=383 mm; Sash Width Sides=383 mm; Standard Interlocker=Yes; Width=1490 mm  [stored 4.88845 ft]; Windload Design=2000 mm  [stored 6.56168 ft]
- 540SW-1509XXXX-1500Pa: Area Middle Sash Glazing=0.19 m²; Area Side Sash Glazing=0.19 m²; Clearvue SHGC Value=0.484; Custom Windload=1500 mm  [stored 4.92126 ft]; Custom Window Height=890 mm  [stored 2.91995 ft]; Custom Window Width=1490 mm  [stored 4.88845 ft]; Energy Advantage SHGC Value=0.438; Energy Advantage U Value=6.17; Heavy Duty Handle=No; Heavy Duty Interlocker=No; Height=890 mm  [stored 2.91995 ft]; Intruderprufe LowE SHGC Value=0.408; Intruderprufe LowE U Value=6.06; Intruderprufe SHGC Value=0.458; Intruderprufe U Value=7.18; Is Heavy Duty Handle=0 mm  [stored 0 ft]; Is Heavy Duty Mullion=0 mm  [stored 0 ft]; Limit Sash Width Side Max=465 mm; Limit Sash Width Side Min=300 mm  [stored 0.984252 ft]; Max Pane Area=0.19 m²; Sash Height=810 mm; Sash Width Middle=383 mm; Sash Width Sides=383 mm; Standard Interlocker=Yes; Width=1490 mm  [stored 4.88845 ft]; Windload Design=1500 mm  [stored 4.92126 ft]
- 540SW-1509XXXX-2000Pa: Area Middle Sash Glazing=0.19 m²; Area Side Sash Glazing=0.19 m²; Clearvue SHGC Value=0.484; Custom Windload=2000 mm  [stored 6.56168 ft]; Custom Window Height=890 mm  [stored 2.91995 ft]; Custom Window Width=1490 mm  [stored 4.88845 ft]; Energy Advantage SHGC Value=0.438; Energy Advantage U Value=6.17; Heavy Duty Handle=No; Heavy Duty Interlocker=No; Height=890 mm  [stored 2.91995 ft]; Intruderprufe LowE SHGC Value=0.408; Intruderprufe LowE U Value=6.06; Intruderprufe SHGC Value=0.458; Intruderprufe U Value=7.18; Is Heavy Duty Handle=0 mm  [stored 0 ft]; Is Heavy Duty Mullion=0 mm  [stored 0 ft]; Limit Sash Width Side Max=465 mm; Limit Sash Width Side Min=300 mm  [stored 0.984252 ft]; Max Pane Area=0.19 m²; Sash Height=810 mm; Sash Width Middle=383 mm; Sash Width Sides=383 mm; Standard Interlocker=Yes; Width=1490 mm  [stored 4.88845 ft]; Windload Design=2000 mm  [stored 6.56168 ft]
- 540SW-1512XXXX-1500Pa: Area Middle Sash Glazing=0.28 m²; Area Side Sash Glazing=0.28 m²; Clearvue SHGC Value=0.518; Custom Windload=1500 mm  [stored 4.92126 ft]; Custom Window Height=1190 mm  [stored 3.9042 ft]; Custom Window Width=1490 mm  [stored 4.88845 ft]; Energy Advantage SHGC Value=0.468; Energy Advantage U Value=6.05; Heavy Duty Handle=No; Heavy Duty Interlocker=No; Height=1190 mm  [stored 3.9042 ft]; Intruderprufe LowE SHGC Value=0.436; Intruderprufe LowE U Value=5.94; Intruderprufe SHGC Value=0.49; Intruderprufe U Value=7.15; Is Heavy Duty Handle=0 mm  [stored 0 ft]; Is Heavy Duty Mullion=0 mm  [stored 0 ft]; Limit Sash Width Side Max=465 mm; Limit Sash Width Side Min=300 mm  [stored 0.984252 ft]; Max Pane Area=0.28 m²; Sash Height=1110 mm; Sash Width Middle=383 mm; Sash Width Sides=383 mm; Standard Interlocker=Yes; Width=1490 mm  [stored 4.88845 ft]; Windload Design=1500 mm  [stored 4.92126 ft]
- 540SW-1512XXXX-2000Pa: Area Middle Sash Glazing=0.28 m²; Area Side Sash Glazing=0.28 m²; Clearvue SHGC Value=0.518; Custom Windload=2000 mm  [stored 6.56168 ft]; Custom Window Height=1190 mm  [stored 3.9042 ft]; Custom Window Width=1490 mm  [stored 4.88845 ft]; Energy Advantage SHGC Value=0.468; Energy Advantage U Value=6.05; Heavy Duty Handle=No; Heavy Duty Interlocker=No; Height=1190 mm  [stored 3.9042 ft]; Intruderprufe LowE SHGC Value=0.436; Intruderprufe LowE U Value=5.94; Intruderprufe SHGC Value=0.49; Intruderprufe U Value=7.15; Is Heavy Duty Handle=0 mm  [stored 0 ft]; Is Heavy Duty Mullion=0 mm  [stored 0 ft]; Limit Sash Width Side Max=465 mm; Limit Sash Width Side Min=300 mm  [stored 0.984252 ft]; Max Pane Area=0.28 m²; Sash Height=1110 mm; Sash Width Middle=383 mm; Sash Width Sides=383 mm; Standard Interlocker=Yes; Width=1490 mm  [stored 4.88845 ft]; Windload Design=2000 mm  [stored 6.56168 ft]
- 540SW-1515XXXX-1500Pa: Area Middle Sash Glazing=0.36 m²; Area Side Sash Glazing=0.36 m²; Clearvue SHGC Value=0.539; Custom Windload=1500 mm  [stored 4.92126 ft]; Custom Window Height=1490 mm  [stored 4.88845 ft]; Custom Window Width=1490 mm  [stored 4.88845 ft]; Energy Advantage SHGC Value=0.486; Energy Advantage U Value=5.97; Heavy Duty Handle=No; Heavy Duty Interlocker=No; Height=1490 mm  [stored 4.88845 ft]; Intruderprufe LowE SHGC Value=0.453; Intruderprufe LowE U Value=5.87; Intruderprufe SHGC Value=0.509; Intruderprufe U Value=7.13; Is Heavy Duty Handle=0 mm  [stored 0 ft]; Is Heavy Duty Mullion=0 mm  [stored 0 ft]; Limit Sash Width Side Max=465 mm; Limit Sash Width Side Min=300 mm  [stored 0.984252 ft]; Max Pane Area=0.36 m²; Sash Height=1410 mm; Sash Width Middle=383 mm; Sash Width Sides=383 mm; Standard Interlocker=Yes; Width=1490 mm  [stored 4.88845 ft]; Windload Design=1500 mm  [stored 4.92126 ft]
- 540SW-1515XXXX-2000Pa: Area Middle Sash Glazing=0.36 m²; Area Side Sash Glazing=0.36 m²; Clearvue SHGC Value=0.539; Custom Windload=2000 mm  [stored 6.56168 ft]; Custom Window Height=1490 mm  [stored 4.88845 ft]; Custom Window Width=1490 mm  [stored 4.88845 ft]; Energy Advantage SHGC Value=0.486; Energy Advantage U Value=5.97; Heavy Duty Handle=Yes; Heavy Duty Interlocker=Yes; Height=1490 mm  [stored 4.88845 ft]; Intruderprufe LowE SHGC Value=0.453; Intruderprufe LowE U Value=5.87; Intruderprufe SHGC Value=0.509; Intruderprufe U Value=7.13; Is Heavy Duty Handle=1 mm  [stored 0.00328084 ft]; Is Heavy Duty Mullion=1 mm  [stored 0.00328084 ft]; Limit Sash Width Side Max=465 mm; Limit Sash Width Side Min=300 mm  [stored 0.984252 ft]; Max Pane Area=0.36 m²; Sash Height=1410 mm; Sash Width Middle=383 mm; Sash Width Sides=383 mm; Standard Interlocker=No; Width=1490 mm  [stored 4.88845 ft]; Windload Design=2000 mm  [stored 6.56168 ft]
- 540SW-2106XXXX-1500Pa: Area Middle Sash Glazing=0.17 m²; Area Side Sash Glazing=0.17 m²; Clearvue SHGC Value=0.457; Custom Windload=1500 mm  [stored 4.92126 ft]; Custom Window Height=590 mm  [stored 1.9357 ft]; Custom Window Width=2090 mm  [stored 6.85696 ft]; Energy Advantage SHGC Value=0.413; Energy Advantage U Value=6.07; Heavy Duty Handle=No; Heavy Duty Interlocker=No; Height=590 mm  [stored 1.9357 ft]; Intruderprufe LowE SHGC Value=0.386; Intruderprufe LowE U Value=5.96; Intruderprufe SHGC Value=0.432; Intruderprufe U Value=7.07; Is Heavy Duty Handle=0 mm  [stored 0 ft]; Is Heavy Duty Mullion=0 mm  [stored 0 ft]; Limit Sash Width Side Max=765 mm; Limit Sash Width Side Min=300 mm  [stored 0.984252 ft]; Max Pane Area=0.17 m²; Sash Height=510 mm; Sash Width Middle=533 mm; Sash Width Sides=533 mm; Standard Interlocker=Yes; Width=2090 mm  [stored 6.85696 ft]; Windload Design=1500 mm  [stored 4.92126 ft]
- 540SW-2106XXXX-2000Pa: Area Middle Sash Glazing=0.17 m²; Area Side Sash Glazing=0.17 m²; Clearvue SHGC Value=0.457; Custom Windload=2000 mm  [stored 6.56168 ft]; Custom Window Height=590 mm  [stored 1.9357 ft]; Custom Window Width=2090 mm  [stored 6.85696 ft]; Energy Advantage SHGC Value=0.413; Energy Advantage U Value=6.07; Heavy Duty Handle=No; Heavy Duty Interlocker=No; Height=590 mm  [stored 1.9357 ft]; Intruderprufe LowE SHGC Value=0.386; Intruderprufe LowE U Value=5.96; Intruderprufe SHGC Value=0.432; Intruderprufe U Value=7.07; Is Heavy Duty Handle=0 mm  [stored 0 ft]; Is Heavy Duty Mullion=0 mm  [stored 0 ft]; Limit Sash Width Side Max=765 mm; Limit Sash Width Side Min=300 mm  [stored 0.984252 ft]; Max Pane Area=0.17 m²; Sash Height=510 mm; Sash Width Middle=533 mm; Sash Width Sides=533 mm; Standard Interlocker=Yes; Width=2090 mm  [stored 6.85696 ft]; Windload Design=2000 mm  [stored 6.56168 ft]
- 540SW-1812XXXX-1500Pa: Area Middle Sash Glazing=0.35 m²; Area Side Sash Glazing=0.35 m²; Clearvue SHGC Value=0.55; Custom Windload=1500 mm  [stored 4.92126 ft]; Custom Window Height=1190 mm  [stored 3.9042 ft]; Custom Window Width=1790 mm  [stored 5.8727 ft]; Energy Advantage SHGC Value=0.495; Energy Advantage U Value=5.78; Heavy Duty Handle=No; Heavy Duty Interlocker=No; Height=1190 mm  [stored 3.9042 ft]; Intruderprufe LowE SHGC Value=0.462; Intruderprufe LowE U Value=5.68; Intruderprufe SHGC Value=0.519; Intruderprufe U Value=6.97; Is Heavy Duty Handle=0 mm  [stored 0 ft]; Is Heavy Duty Mullion=0 mm  [stored 0 ft]; Limit Sash Width Side Max=615 mm; Limit Sash Width Side Min=300 mm  [stored 0.984252 ft]; Max Pane Area=0.35 m²; Sash Height=1110 mm; Sash Width Middle=458 mm; Sash Width Sides=458 mm; Standard Interlocker=Yes; Width=1790 mm  [stored 5.8727 ft]; Windload Design=1500 mm  [stored 4.92126 ft]
- 540SW-1812XXXX-2000Pa: Area Middle Sash Glazing=0.35 m²; Area Side Sash Glazing=0.35 m²; Clearvue SHGC Value=0.55; Custom Windload=2000 mm  [stored 6.56168 ft]; Custom Window Height=1190 mm  [stored 3.9042 ft]; Custom Window Width=1790 mm  [stored 5.8727 ft]; Energy Advantage SHGC Value=0.495; Energy Advantage U Value=5.78; Heavy Duty Handle=No; Heavy Duty Interlocker=No; Height=1190 mm  [stored 3.9042 ft]; Intruderprufe LowE SHGC Value=0.462; Intruderprufe LowE U Value=5.68; Intruderprufe SHGC Value=0.519; Intruderprufe U Value=6.97; Is Heavy Duty Handle=0 mm  [stored 0 ft]; Is Heavy Duty Mullion=0 mm  [stored 0 ft]; Limit Sash Width Side Max=615 mm; Limit Sash Width Side Min=300 mm  [stored 0.984252 ft]; Max Pane Area=0.35 m²; Sash Height=1110 mm; Sash Width Middle=458 mm; Sash Width Sides=458 mm; Standard Interlocker=Yes; Width=1790 mm  [stored 5.8727 ft]; Windload Design=2000 mm  [stored 6.56168 ft]
- 540SW-1809XXXX-1500Pa: Area Middle Sash Glazing=0.25 m²; Area Side Sash Glazing=0.25 m²; Clearvue SHGC Value=0.513; Custom Windload=1500 mm  [stored 4.92126 ft]; Custom Window Height=890 mm  [stored 2.91995 ft]; Custom Window Width=1790 mm  [stored 5.8727 ft]; Energy Advantage SHGC Value=0.463; Energy Advantage U Value=5.92; Heavy Duty Handle=No; Heavy Duty Interlocker=No; Height=890 mm  [stored 2.91995 ft]; Intruderprufe LowE SHGC Value=0.432; Intruderprufe LowE U Value=5.82; Intruderprufe SHGC Value=0.485; Intruderprufe U Value=7.02; Is Heavy Duty Handle=0 mm  [stored 0 ft]; Is Heavy Duty Mullion=0 mm  [stored 0 ft]; Limit Sash Width Side Max=615 mm; Limit Sash Width Side Min=300 mm  [stored 0.984252 ft]; Max Pane Area=0.25 m²; Sash Height=810 mm; Sash Width Middle=458 mm; Sash Width Sides=458 mm; Standard Interlocker=Yes; Width=1790 mm  [stored 5.8727 ft]; Windload Design=1500 mm  [stored 4.92126 ft]
- 540SW-1809XXXX-2000Pa: Area Middle Sash Glazing=0.25 m²; Area Side Sash Glazing=0.25 m²; Clearvue SHGC Value=0.513; Custom Windload=2000 mm  [stored 6.56168 ft]; Custom Window Height=890 mm  [stored 2.91995 ft]; Custom Window Width=1790 mm  [stored 5.8727 ft]; Energy Advantage SHGC Value=0.463; Energy Advantage U Value=5.92; Heavy Duty Handle=No; Heavy Duty Interlocker=No; Height=890 mm  [stored 2.91995 ft]; Intruderprufe LowE SHGC Value=0.432; Intruderprufe LowE U Value=5.82; Intruderprufe SHGC Value=0.485; Intruderprufe U Value=7.02; Is Heavy Duty Handle=0 mm  [stored 0 ft]; Is Heavy Duty Mullion=0 mm  [stored 0 ft]; Limit Sash Width Side Max=615 mm; Limit Sash Width Side Min=300 mm  [stored 0.984252 ft]; Max Pane Area=0.25 m²; Sash Height=810 mm; Sash Width Middle=458 mm; Sash Width Sides=458 mm; Standard Interlocker=Yes; Width=1790 mm  [stored 5.8727 ft]; Windload Design=2000 mm  [stored 6.56168 ft]
- 540SW-1815XXXX-1500Pa: Area Middle Sash Glazing=0.46 m²; Area Side Sash Glazing=0.46 m²; Clearvue SHGC Value=0.572; Custom Windload=1500 mm  [stored 4.92126 ft]; Custom Window Height=1490 mm  [stored 4.88845 ft]; Custom Window Width=1790 mm  [stored 5.8727 ft]; Energy Advantage SHGC Value=0.515; Energy Advantage U Value=5.69; Heavy Duty Handle=Yes; Heavy Duty Interlocker=Yes; Height=1490 mm  [stored 4.88845 ft]; Intruderprufe LowE SHGC Value=0.479; Intruderprufe LowE U Value=5.59; Intruderprufe SHGC Value=0.54; Intruderprufe U Value=6.94; Is Heavy Duty Handle=1 mm  [stored 0.00328084 ft]; Is Heavy Duty Mullion=1 mm  [stored 0.00328084 ft]; Limit Sash Width Side Max=615 mm; Limit Sash Width Side Min=300 mm  [stored 0.984252 ft]; Max Pane Area=0.46 m²; Sash Height=1410 mm; Sash Width Middle=458 mm; Sash Width Sides=458 mm; Standard Interlocker=No; Width=1790 mm  [stored 5.8727 ft]; Windload Design=1500 mm  [stored 4.92126 ft]
- 540SW-1815XXXX-2000Pa: Area Middle Sash Glazing=0.46 m²; Area Side Sash Glazing=0.46 m²; Clearvue SHGC Value=0.572; Custom Windload=2000 mm  [stored 6.56168 ft]; Custom Window Height=1490 mm  [stored 4.88845 ft]; Custom Window Width=1790 mm  [stored 5.8727 ft]; Energy Advantage SHGC Value=0.515; Energy Advantage U Value=5.69; Heavy Duty Handle=Yes; Heavy Duty Interlocker=Yes; Height=1490 mm  [stored 4.88845 ft]; Intruderprufe LowE SHGC Value=0.479; Intruderprufe LowE U Value=5.59; Intruderprufe SHGC Value=0.54; Intruderprufe U Value=6.94; Is Heavy Duty Handle=1 mm  [stored 0.00328084 ft]; Is Heavy Duty Mullion=1 mm  [stored 0.00328084 ft]; Limit Sash Width Side Max=615 mm; Limit Sash Width Side Min=300 mm  [stored 0.984252 ft]; Max Pane Area=0.46 m²; Sash Height=1410 mm; Sash Width Middle=458 mm; Sash Width Sides=458 mm; Standard Interlocker=No; Width=1790 mm  [stored 5.8727 ft]; Windload Design=2000 mm  [stored 6.56168 ft]
- 540SW-2109XXXX-1500Pa: Area Middle Sash Glazing=0.3 m²; Area Side Sash Glazing=0.3 m²; Clearvue SHGC Value=0.534; Custom Windload=1500 mm  [stored 4.92126 ft]; Custom Window Height=890 mm  [stored 2.91995 ft]; Custom Window Width=2090 mm  [stored 6.85696 ft]; Energy Advantage SHGC Value=0.481; Energy Advantage U Value=5.75; Heavy Duty Handle=No; Heavy Duty Interlocker=No; Height=890 mm  [stored 2.91995 ft]; Intruderprufe LowE SHGC Value=0.449; Intruderprufe LowE U Value=5.64; Intruderprufe SHGC Value=0.504; Intruderprufe U Value=6.9; Is Heavy Duty Handle=0 mm  [stored 0 ft]; Is Heavy Duty Mullion=0 mm  [stored 0 ft]; Limit Sash Width Side Max=765 mm; Limit Sash Width Side Min=300 mm  [stored 0.984252 ft]; Max Pane Area=0.3 m²; Sash Height=810 mm; Sash Width Middle=533 mm; Sash Width Sides=533 mm; Standard Interlocker=Yes; Width=2090 mm  [stored 6.85696 ft]; Windload Design=1500 mm  [stored 4.92126 ft]
- 540SW-2109XXXX-2000Pa: Area Middle Sash Glazing=0.3 m²; Area Side Sash Glazing=0.3 m²; Clearvue SHGC Value=0.534; Custom Windload=2000 mm  [stored 6.56168 ft]; Custom Window Height=890 mm  [stored 2.91995 ft]; Custom Window Width=2090 mm  [stored 6.85696 ft]; Energy Advantage SHGC Value=0.481; Energy Advantage U Value=5.75; Heavy Duty Handle=No; Heavy Duty Interlocker=No; Height=890 mm  [stored 2.91995 ft]; Intruderprufe LowE SHGC Value=0.449; Intruderprufe LowE U Value=5.64; Intruderprufe SHGC Value=0.504; Intruderprufe U Value=6.9; Is Heavy Duty Handle=0 mm  [stored 0 ft]; Is Heavy Duty Mullion=0 mm  [stored 0 ft]; Limit Sash Width Side Max=765 mm; Limit Sash Width Side Min=300 mm  [stored 0.984252 ft]; Max Pane Area=0.3 m²; Sash Height=810 mm; Sash Width Middle=533 mm; Sash Width Sides=533 mm; Standard Interlocker=Yes; Width=2090 mm  [stored 6.85696 ft]; Windload Design=2000 mm  [stored 6.56168 ft]
- 540SW-2112XXXX-1500Pa: Area Middle Sash Glazing=0.43 m²; Area Side Sash Glazing=0.43 m²; Clearvue SHGC Value=0.572; Custom Windload=1500 mm  [stored 4.92126 ft]; Custom Window Height=1190 mm  [stored 3.9042 ft]; Custom Window Width=2090 mm  [stored 6.85696 ft]; Energy Advantage SHGC Value=0.515; Energy Advantage U Value=5.59; Heavy Duty Handle=No; Heavy Duty Interlocker=No; Height=1190 mm  [stored 3.9042 ft]; Intruderprufe LowE SHGC Value=0.48; Intruderprufe LowE U Value=4.59; Intruderprufe SHGC Value=0.54; Intruderprufe U Value=6.85; Is Heavy Duty Handle=0 mm  [stored 0 ft]; Is Heavy Duty Mullion=0 mm  [stored 0 ft]; Limit Sash Width Side Max=765 mm; Limit Sash Width Side Min=300 mm  [stored 0.984252 ft]; Max Pane Area=0.43 m²; Sash Height=1110 mm; Sash Width Middle=533 mm; Sash Width Sides=533 mm; Standard Interlocker=Yes; Width=2090 mm  [stored 6.85696 ft]; Windload Design=1500 mm  [stored 4.92126 ft]
- 540SW-2112XXXX-2000Pa: Area Middle Sash Glazing=0.43 m²; Area Side Sash Glazing=0.43 m²; Clearvue SHGC Value=0.572; Custom Windload=2000 mm  [stored 6.56168 ft]; Custom Window Height=1190 mm  [stored 3.9042 ft]; Custom Window Width=2090 mm  [stored 6.85696 ft]; Energy Advantage SHGC Value=0.515; Energy Advantage U Value=5.59; Heavy Duty Handle=No; Heavy Duty Interlocker=No; Height=1190 mm  [stored 3.9042 ft]; Intruderprufe LowE SHGC Value=0.48; Intruderprufe LowE U Value=4.59; Intruderprufe SHGC Value=0.54; Intruderprufe U Value=6.85; Is Heavy Duty Handle=0 mm  [stored 0 ft]; Is Heavy Duty Mullion=0 mm  [stored 0 ft]; Limit Sash Width Side Max=765 mm; Limit Sash Width Side Min=300 mm  [stored 0.984252 ft]; Max Pane Area=0.43 m²; Sash Height=1110 mm; Sash Width Middle=533 mm; Sash Width Sides=533 mm; Standard Interlocker=Yes; Width=2090 mm  [stored 6.85696 ft]; Windload Design=2000 mm  [stored 6.56168 ft]
- 540SW-2115XXXX-1500Pa: Area Middle Sash Glazing=0.55 m²; Area Side Sash Glazing=0.55 m²; Clearvue SHGC Value=0.595; Custom Windload=1500 mm  [stored 4.92126 ft]; Custom Window Height=1490 mm  [stored 4.88845 ft]; Custom Window Width=2090 mm  [stored 6.85696 ft]; Energy Advantage SHGC Value=0.535; Energy Advantage U Value=5.49; Heavy Duty Handle=Yes; Heavy Duty Interlocker=Yes; Height=1490 mm  [stored 4.88845 ft]; Intruderprufe LowE SHGC Value=0.498; Intruderprufe LowE U Value=5.39; Intruderprufe SHGC Value=0.562; Intruderprufe U Value=6.81; Is Heavy Duty Handle=1 mm  [stored 0.00328084 ft]; Is Heavy Duty Mullion=1 mm  [stored 0.00328084 ft]; Limit Sash Width Side Max=765 mm; Limit Sash Width Side Min=300 mm  [stored 0.984252 ft]; Max Pane Area=0.55 m²; Sash Height=1410 mm; Sash Width Middle=533 mm; Sash Width Sides=533 mm; Standard Interlocker=No; Width=2090 mm  [stored 6.85696 ft]; Windload Design=1500 mm  [stored 4.92126 ft]
- 540SW-2115XXXX-2000Pa: Area Middle Sash Glazing=0.55 m²; Area Side Sash Glazing=0.55 m²; Clearvue SHGC Value=0.595; Custom Windload=2000 mm  [stored 6.56168 ft]; Custom Window Height=1490 mm  [stored 4.88845 ft]; Custom Window Width=2090 mm  [stored 6.85696 ft]; Energy Advantage SHGC Value=0.535; Energy Advantage U Value=5.49; Heavy Duty Handle=Yes; Heavy Duty Interlocker=Yes; Height=1490 mm  [stored 4.88845 ft]; Intruderprufe LowE SHGC Value=0.498; Intruderprufe LowE U Value=5.39; Intruderprufe SHGC Value=0.562; Intruderprufe U Value=6.81; Is Heavy Duty Handle=1 mm  [stored 0.00328084 ft]; Is Heavy Duty Mullion=1 mm  [stored 0.00328084 ft]; Limit Sash Width Side Max=765 mm; Limit Sash Width Side Min=300 mm  [stored 0.984252 ft]; Max Pane Area=0.55 m²; Sash Height=1410 mm; Sash Width Middle=533 mm; Sash Width Sides=533 mm; Standard Interlocker=No; Width=2090 mm  [stored 6.85696 ft]; Windload Design=2000 mm  [stored 6.56168 ft]
- 540SW-2406XXXX-1500Pa: Area Middle Sash Glazing=0.2 m²; Area Side Sash Glazing=0.2 m²; Clearvue SHGC Value=0.47; Custom Windload=1500 mm  [stored 4.92126 ft]; Custom Window Height=590 mm  [stored 1.9357 ft]; Custom Window Width=2390 mm  [stored 7.84121 ft]; Energy Advantage SHGC Value=0.424; Energy Advantage U Value=5.96; Heavy Duty Handle=No; Heavy Duty Interlocker=No; Height=590 mm  [stored 1.9357 ft]; Intruderprufe LowE SHGC Value=0.397; Intruderprufe LowE U Value=5.86; Intruderprufe SHGC Value=0.444; Intruderprufe U Value=6.94; Is Heavy Duty Handle=0 mm  [stored 0 ft]; Is Heavy Duty Mullion=0 mm  [stored 0 ft]; Limit Sash Width Side Max=915 mm; Limit Sash Width Side Min=300 mm  [stored 0.984252 ft]; Max Pane Area=0.2 m²; Sash Height=510 mm; Sash Width Middle=608 mm; Sash Width Sides=608 mm; Standard Interlocker=Yes; Width=2390 mm  [stored 7.84121 ft]; Windload Design=1500 mm  [stored 4.92126 ft]
- 540SW-2406XXXX-2000Pa: Area Middle Sash Glazing=0.2 m²; Area Side Sash Glazing=0.2 m²; Clearvue SHGC Value=0.47; Custom Windload=2000 mm  [stored 6.56168 ft]; Custom Window Height=590 mm  [stored 1.9357 ft]; Custom Window Width=2390 mm  [stored 7.84121 ft]; Energy Advantage SHGC Value=0.424; Energy Advantage U Value=5.96; Heavy Duty Handle=No; Heavy Duty Interlocker=No; Height=590 mm  [stored 1.9357 ft]; Intruderprufe LowE SHGC Value=0.397; Intruderprufe LowE U Value=5.86; Intruderprufe SHGC Value=0.444; Intruderprufe U Value=6.94; Is Heavy Duty Handle=0 mm  [stored 0 ft]; Is Heavy Duty Mullion=0 mm  [stored 0 ft]; Limit Sash Width Side Max=915 mm; Limit Sash Width Side Min=300 mm  [stored 0.984252 ft]; Max Pane Area=0.2 m²; Sash Height=510 mm; Sash Width Middle=608 mm; Sash Width Sides=608 mm; Standard Interlocker=Yes; Width=2390 mm  [stored 7.84121 ft]; Windload Design=2000 mm  [stored 6.56168 ft]
- 540SW-2409XXXX-1500Pa: Area Middle Sash Glazing=0.35 m²; Area Side Sash Glazing=0.35 m²; Clearvue SHGC Value=0.55; Custom Windload=1500 mm  [stored 4.92126 ft]; Custom Window Height=890 mm  [stored 2.91995 ft]; Custom Window Width=2390 mm  [stored 7.84121 ft]; Energy Advantage SHGC Value=0.495; Energy Advantage U Value=5.61; Heavy Duty Handle=No; Heavy Duty Interlocker=No; Height=890 mm  [stored 2.91995 ft]; Intruderprufe LowE SHGC Value=0.461; Intruderprufe LowE U Value=5.51; Intruderprufe SHGC Value=0.519; Intruderprufe U Value=6.82; Is Heavy Duty Handle=0 mm  [stored 0 ft]; Is Heavy Duty Mullion=0 mm  [stored 0 ft]; Limit Sash Width Side Max=915 mm; Limit Sash Width Side Min=300 mm  [stored 0.984252 ft]; Max Pane Area=0.35 m²; Sash Height=810 mm; Sash Width Middle=608 mm; Sash Width Sides=608 mm; Standard Interlocker=Yes; Width=2390 mm  [stored 7.84121 ft]; Windload Design=1500 mm  [stored 4.92126 ft]
- 540SW-2409XXXX-2000Pa: Area Middle Sash Glazing=0.35 m²; Area Side Sash Glazing=0.35 m²; Clearvue SHGC Value=0.55; Custom Windload=2000 mm  [stored 6.56168 ft]; Custom Window Height=890 mm  [stored 2.91995 ft]; Custom Window Width=2390 mm  [stored 7.84121 ft]; Energy Advantage SHGC Value=0.495; Energy Advantage U Value=5.61; Heavy Duty Handle=No; Heavy Duty Interlocker=No; Height=890 mm  [stored 2.91995 ft]; Intruderprufe LowE SHGC Value=0.461; Intruderprufe LowE U Value=5.51; Intruderprufe SHGC Value=0.519; Intruderprufe U Value=6.82; Is Heavy Duty Handle=0 mm  [stored 0 ft]; Is Heavy Duty Mullion=0 mm  [stored 0 ft]; Limit Sash Width Side Max=915 mm; Limit Sash Width Side Min=300 mm  [stored 0.984252 ft]; Max Pane Area=0.35 m²; Sash Height=810 mm; Sash Width Middle=608 mm; Sash Width Sides=608 mm; Standard Interlocker=Yes; Width=2390 mm  [stored 7.84121 ft]; Windload Design=2000 mm  [stored 6.56168 ft]
- 540SW-2412XXXX-1500Pa: Area Middle Sash Glazing=0.5 m²; Area Side Sash Glazing=0.5 m²; Clearvue SHGC Value=0.589; Custom Windload=1500 mm  [stored 4.92126 ft]; Custom Window Height=1190 mm  [stored 3.9042 ft]; Custom Window Width=2390 mm  [stored 7.84121 ft]; Energy Advantage SHGC Value=0.53; Energy Advantage U Value=5.44; Heavy Duty Handle=No; Heavy Duty Interlocker=No; Height=1190 mm  [stored 3.9042 ft]; Intruderprufe LowE SHGC Value=0.494; Intruderprufe LowE U Value=5.35; Intruderprufe SHGC Value=0.556; Intruderprufe U Value=6.75; Is Heavy Duty Handle=0 mm  [stored 0 ft]; Is Heavy Duty Mullion=0 mm  [stored 0 ft]; Limit Sash Width Side Max=915 mm; Limit Sash Width Side Min=300 mm  [stored 0.984252 ft]; Max Pane Area=0.5 m²; Sash Height=1110 mm; Sash Width Middle=608 mm; Sash Width Sides=608 mm; Standard Interlocker=Yes; Width=2390 mm  [stored 7.84121 ft]; Windload Design=1500 mm  [stored 4.92126 ft]
- 540SW-2412XXXX-2000Pa: Area Middle Sash Glazing=0.5 m²; Area Side Sash Glazing=0.5 m²; Clearvue SHGC Value=0.589; Custom Windload=2000 mm  [stored 6.56168 ft]; Custom Window Height=1190 mm  [stored 3.9042 ft]; Custom Window Width=2390 mm  [stored 7.84121 ft]; Energy Advantage SHGC Value=0.53; Energy Advantage U Value=5.44; Heavy Duty Handle=No; Heavy Duty Interlocker=No; Height=1190 mm  [stored 3.9042 ft]; Intruderprufe LowE SHGC Value=0.494; Intruderprufe LowE U Value=5.35; Intruderprufe SHGC Value=0.556; Intruderprufe U Value=6.75; Is Heavy Duty Handle=0 mm  [stored 0 ft]; Is Heavy Duty Mullion=0 mm  [stored 0 ft]; Limit Sash Width Side Max=915 mm; Limit Sash Width Side Min=300 mm  [stored 0.984252 ft]; Max Pane Area=0.5 m²; Sash Height=1110 mm; Sash Width Middle=608 mm; Sash Width Sides=608 mm; Standard Interlocker=Yes; Width=2390 mm  [stored 7.84121 ft]; Windload Design=2000 mm  [stored 6.56168 ft]
- 540SW-2415XXXX-1500Pa: Area Middle Sash Glazing=0.65 m²; Area Side Sash Glazing=0.65 m²; Clearvue SHGC Value=0.613; Custom Windload=1500 mm  [stored 4.92126 ft]; Custom Window Height=1490 mm  [stored 4.88845 ft]; Custom Window Width=2390 mm  [stored 7.84121 ft]; Energy Advantage SHGC Value=0.551; Energy Advantage U Value=5.34; Heavy Duty Handle=Yes; Heavy Duty Interlocker=Yes; Height=1490 mm  [stored 4.88845 ft]; Intruderprufe LowE SHGC Value=0.513; Intruderprufe LowE U Value=5.24; Intruderprufe SHGC Value=0.578; Intruderprufe U Value=6.72; Is Heavy Duty Handle=1 mm  [stored 0.00328084 ft]; Is Heavy Duty Mullion=1 mm  [stored 0.00328084 ft]; Limit Sash Width Side Max=915 mm; Limit Sash Width Side Min=300 mm  [stored 0.984252 ft]; Max Pane Area=0.65 m²; Sash Height=1410 mm; Sash Width Middle=608 mm; Sash Width Sides=608 mm; Standard Interlocker=No; Width=2390 mm  [stored 7.84121 ft]; Windload Design=1500 mm  [stored 4.92126 ft]
- 540SW-2415XXXX-2000Pa: Area Middle Sash Glazing=0.65 m²; Area Side Sash Glazing=0.65 m²; Clearvue SHGC Value=0.613; Custom Windload=2000 mm  [stored 6.56168 ft]; Custom Window Height=1490 mm  [stored 4.88845 ft]; Custom Window Width=2390 mm  [stored 7.84121 ft]; Energy Advantage SHGC Value=0.551; Energy Advantage U Value=5.34; Heavy Duty Handle=Yes; Heavy Duty Interlocker=Yes; Height=1490 mm  [stored 4.88845 ft]; Intruderprufe LowE SHGC Value=0.513; Intruderprufe LowE U Value=5.24; Intruderprufe SHGC Value=0.578; Intruderprufe U Value=6.72; Is Heavy Duty Handle=1 mm  [stored 0.00328084 ft]; Is Heavy Duty Mullion=1 mm  [stored 0.00328084 ft]; Limit Sash Width Side Max=915 mm; Limit Sash Width Side Min=300 mm  [stored 0.984252 ft]; Max Pane Area=0.65 m²; Sash Height=1410 mm; Sash Width Middle=608 mm; Sash Width Sides=608 mm; Standard Interlocker=No; Width=2390 mm  [stored 7.84121 ft]; Windload Design=2000 mm  [stored 6.56168 ft]
- 540SW-2706XXXX-1500Pa: Area Middle Sash Glazing=0.23 m²; Area Side Sash Glazing=0.23 m²; Clearvue SHGC Value=0.48; Custom Windload=1500 mm  [stored 4.92126 ft]; Custom Window Height=590 mm  [stored 1.9357 ft]; Custom Window Width=2690 mm; Energy Advantage SHGC Value=0.433; Energy Advantage U Value=5.87; Heavy Duty Handle=No; Heavy Duty Interlocker=No; Height=590 mm  [stored 1.9357 ft]; Intruderprufe LowE SHGC Value=0.405; Intruderprufe LowE U Value=5.77; Intruderprufe SHGC Value=0.454; Intruderprufe U Value=6.89; Is Heavy Duty Handle=0 mm  [stored 0 ft]; Is Heavy Duty Mullion=0 mm  [stored 0 ft]; Limit Sash Width Side Max=1065 mm; Limit Sash Width Side Min=300 mm  [stored 0.984252 ft]; Max Pane Area=0.23 m²; Sash Height=510 mm; Sash Width Middle=683 mm; Sash Width Sides=683 mm; Standard Interlocker=Yes; Width=2690 mm; Windload Design=1500 mm  [stored 4.92126 ft]
- 540SW-2706XXXX-2000Pa: Area Middle Sash Glazing=0.23 m²; Area Side Sash Glazing=0.23 m²; Clearvue SHGC Value=0.48; Custom Windload=2000 mm  [stored 6.56168 ft]; Custom Window Height=590 mm  [stored 1.9357 ft]; Custom Window Width=2690 mm; Energy Advantage SHGC Value=0.433; Energy Advantage U Value=5.87; Heavy Duty Handle=No; Heavy Duty Interlocker=No; Height=590 mm  [stored 1.9357 ft]; Intruderprufe LowE SHGC Value=0.405; Intruderprufe LowE U Value=5.77; Intruderprufe SHGC Value=0.454; Intruderprufe U Value=6.89; Is Heavy Duty Handle=0 mm  [stored 0 ft]; Is Heavy Duty Mullion=0 mm  [stored 0 ft]; Limit Sash Width Side Max=1065 mm; Limit Sash Width Side Min=300 mm  [stored 0.984252 ft]; Max Pane Area=0.23 m²; Sash Height=510 mm; Sash Width Middle=683 mm; Sash Width Sides=683 mm; Standard Interlocker=Yes; Width=2690 mm; Windload Design=2000 mm  [stored 6.56168 ft]
- 540SW-2709XXXX-1500Pa: Area Middle Sash Glazing=0.4 m²; Area Side Sash Glazing=0.4 m²; Clearvue SHGC Value=0.562; Custom Windload=1500 mm  [stored 4.92126 ft]; Custom Window Height=890 mm  [stored 2.91995 ft]; Custom Window Width=2690 mm; Energy Advantage SHGC Value=0.505; Energy Advantage U Value=5.51; Heavy Duty Handle=No; Heavy Duty Interlocker=No; Height=890 mm  [stored 2.91995 ft]; Intruderprufe LowE SHGC Value=0.471; Intruderprufe LowE U Value=5.41; Intruderprufe SHGC Value=0.53; Intruderprufe U Value=6.75; Is Heavy Duty Handle=0 mm  [stored 0 ft]; Is Heavy Duty Mullion=0 mm  [stored 0 ft]; Limit Sash Width Side Max=1065 mm; Limit Sash Width Side Min=300 mm  [stored 0.984252 ft]; Max Pane Area=0.4 m²; Sash Height=810 mm; Sash Width Middle=683 mm; Sash Width Sides=683 mm; Standard Interlocker=Yes; Width=2690 mm; Windload Design=1500 mm  [stored 4.92126 ft]
- 540SW-2709XXXX-2000Pa: Area Middle Sash Glazing=0.4 m²; Area Side Sash Glazing=0.4 m²; Clearvue SHGC Value=0.562; Custom Windload=2000 mm  [stored 6.56168 ft]; Custom Window Height=890 mm  [stored 2.91995 ft]; Custom Window Width=2690 mm; Energy Advantage SHGC Value=0.505; Energy Advantage U Value=5.51; Heavy Duty Handle=No; Heavy Duty Interlocker=No; Height=890 mm  [stored 2.91995 ft]; Intruderprufe LowE SHGC Value=0.471; Intruderprufe LowE U Value=5.41; Intruderprufe SHGC Value=0.53; Intruderprufe U Value=6.75; Is Heavy Duty Handle=0 mm  [stored 0 ft]; Is Heavy Duty Mullion=0 mm  [stored 0 ft]; Limit Sash Width Side Max=1065 mm; Limit Sash Width Side Min=300 mm  [stored 0.984252 ft]; Max Pane Area=0.4 m²; Sash Height=810 mm; Sash Width Middle=683 mm; Sash Width Sides=683 mm; Standard Interlocker=Yes; Width=2690 mm; Windload Design=2000 mm  [stored 6.56168 ft]
- 540SW-2712XXXX-1500Pa: Area Middle Sash Glazing=0.58 m²; Area Side Sash Glazing=0.58 m²; Clearvue SHGC Value=0.602; Custom Windload=1500 mm  [stored 4.92126 ft]; Custom Window Height=1190 mm  [stored 3.9042 ft]; Custom Window Width=2690 mm; Energy Advantage SHGC Value=0.541; Energy Advantage U Value=5.33; Heavy Duty Handle=No; Heavy Duty Interlocker=No; Height=1190 mm  [stored 3.9042 ft]; Intruderprufe LowE SHGC Value=0.504; Intruderprufe LowE U Value=5.24; Intruderprufe SHGC Value=0.568; Intruderprufe U Value=6.68; Is Heavy Duty Handle=0 mm  [stored 0 ft]; Is Heavy Duty Mullion=0 mm  [stored 0 ft]; Limit Sash Width Side Max=1065 mm; Limit Sash Width Side Min=300 mm  [stored 0.984252 ft]; Max Pane Area=0.58 m²; Sash Height=1110 mm; Sash Width Middle=683 mm; Sash Width Sides=683 mm; Standard Interlocker=Yes; Width=2690 mm; Windload Design=1500 mm  [stored 4.92126 ft]
- 540SW-2712XXXX-2000Pa: Area Middle Sash Glazing=0.58 m²; Area Side Sash Glazing=0.58 m²; Clearvue SHGC Value=0.602; Custom Windload=2000 mm  [stored 6.56168 ft]; Custom Window Height=1190 mm  [stored 3.9042 ft]; Custom Window Width=2690 mm; Energy Advantage SHGC Value=0.541; Energy Advantage U Value=5.33; Heavy Duty Handle=No; Heavy Duty Interlocker=No; Height=1190 mm  [stored 3.9042 ft]; Intruderprufe LowE SHGC Value=0.504; Intruderprufe LowE U Value=5.24; Intruderprufe SHGC Value=0.568; Intruderprufe U Value=6.68; Is Heavy Duty Handle=0 mm  [stored 0 ft]; Is Heavy Duty Mullion=0 mm  [stored 0 ft]; Limit Sash Width Side Max=1065 mm; Limit Sash Width Side Min=300 mm  [stored 0.984252 ft]; Max Pane Area=0.58 m²; Sash Height=1110 mm; Sash Width Middle=683 mm; Sash Width Sides=683 mm; Standard Interlocker=Yes; Width=2690 mm; Windload Design=2000 mm  [stored 6.56168 ft]
- 540SW-2715XXXX-1500Pa: Area Middle Sash Glazing=0.75 m²; Area Side Sash Glazing=0.75 m²; Clearvue SHGC Value=0.627; Custom Windload=1500 mm  [stored 4.92126 ft]; Custom Window Height=1490 mm  [stored 4.88845 ft]; Custom Window Width=2690 mm; Energy Advantage SHGC Value=0.563; Energy Advantage U Value=5.22; Heavy Duty Handle=Yes; Heavy Duty Interlocker=Yes; Height=1490 mm  [stored 4.88845 ft]; Intruderprufe LowE SHGC Value=0.524; Intruderprufe LowE U Value=5.13; Intruderprufe SHGC Value=0.591; Intruderprufe U Value=6.64; Is Heavy Duty Handle=1 mm  [stored 0.00328084 ft]; Is Heavy Duty Mullion=1 mm  [stored 0.00328084 ft]; Limit Sash Width Side Max=1065 mm; Limit Sash Width Side Min=300 mm  [stored 0.984252 ft]; Max Pane Area=0.75 m²; Sash Height=1410 mm; Sash Width Middle=683 mm; Sash Width Sides=683 mm; Standard Interlocker=No; Width=2690 mm; Windload Design=1500 mm  [stored 4.92126 ft]
- 540SW-2715XXXX-2000Pa: Area Middle Sash Glazing=0.75 m²; Area Side Sash Glazing=0.75 m²; Clearvue SHGC Value=0.627; Custom Windload=2000 mm  [stored 6.56168 ft]; Custom Window Height=1490 mm  [stored 4.88845 ft]; Custom Window Width=2690 mm; Energy Advantage SHGC Value=0.563; Energy Advantage U Value=5.22; Heavy Duty Handle=Yes; Heavy Duty Interlocker=Yes; Height=1490 mm  [stored 4.88845 ft]; Intruderprufe LowE SHGC Value=0.524; Intruderprufe LowE U Value=5.13; Intruderprufe SHGC Value=0.591; Intruderprufe U Value=6.64; Is Heavy Duty Handle=1 mm  [stored 0.00328084 ft]; Is Heavy Duty Mullion=1 mm  [stored 0.00328084 ft]; Limit Sash Width Side Max=1065 mm; Limit Sash Width Side Min=300 mm  [stored 0.984252 ft]; Max Pane Area=0.75 m²; Sash Height=1410 mm; Sash Width Middle=683 mm; Sash Width Sides=683 mm; Standard Interlocker=No; Width=2690 mm; Windload Design=2000 mm  [stored 6.56168 ft]
- 540SW-3006XXXX-1500Pa: Area Middle Sash Glazing=0.26 m²; Area Side Sash Glazing=0.26 m²; Clearvue SHGC Value=0.488; Custom Windload=1500 mm  [stored 4.92126 ft]; Custom Window Height=590 mm  [stored 1.9357 ft]; Custom Window Width=2990 mm  [stored 9.80971 ft]; Energy Advantage SHGC Value=0.44; Energy Advantage U Value=5.8; Heavy Duty Handle=No; Heavy Duty Interlocker=No; Height=590 mm  [stored 1.9357 ft]; Intruderprufe LowE SHGC Value=0.411; Intruderprufe LowE U Value=5.71; Intruderprufe SHGC Value=0.461; Intruderprufe U Value=6.84; Is Heavy Duty Handle=0 mm  [stored 0 ft]; Is Heavy Duty Mullion=0 mm  [stored 0 ft]; Limit Sash Width Side Max=1200 mm; Limit Sash Width Side Min=315 mm; Max Pane Area=0.26 m²; Sash Height=510 mm; Sash Width Middle=758 mm; Sash Width Sides=758 mm; Standard Interlocker=Yes; Width=2990 mm  [stored 9.80971 ft]; Windload Design=1500 mm  [stored 4.92126 ft]
- 540SW-3006XXXX-2000Pa: Area Middle Sash Glazing=0.26 m²; Area Side Sash Glazing=0.26 m²; Clearvue SHGC Value=0.488; Custom Windload=2000 mm  [stored 6.56168 ft]; Custom Window Height=590 mm  [stored 1.9357 ft]; Custom Window Width=2990 mm  [stored 9.80971 ft]; Energy Advantage SHGC Value=0.44; Energy Advantage U Value=5.8; Heavy Duty Handle=No; Heavy Duty Interlocker=No; Height=590 mm  [stored 1.9357 ft]; Intruderprufe LowE SHGC Value=0.411; Intruderprufe LowE U Value=5.71; Intruderprufe SHGC Value=0.461; Intruderprufe U Value=6.84; Is Heavy Duty Handle=0 mm  [stored 0 ft]; Is Heavy Duty Mullion=0 mm  [stored 0 ft]; Limit Sash Width Side Max=1200 mm; Limit Sash Width Side Min=315 mm; Max Pane Area=0.26 m²; Sash Height=510 mm; Sash Width Middle=758 mm; Sash Width Sides=758 mm; Standard Interlocker=Yes; Width=2990 mm  [stored 9.80971 ft]; Windload Design=2000 mm  [stored 6.56168 ft]
- 540SW-3009XXXX-1500Pa: Area Middle Sash Glazing=0.46 m²; Area Side Sash Glazing=0.46 m²; Clearvue SHGC Value=0.572; Custom Windload=1500 mm  [stored 4.92126 ft]; Custom Window Height=890 mm  [stored 2.91995 ft]; Custom Window Width=2990 mm  [stored 9.80971 ft]; Energy Advantage SHGC Value=0.514; Energy Advantage U Value=5.43; Heavy Duty Handle=No; Heavy Duty Interlocker=No; Height=890 mm  [stored 2.91995 ft]; Intruderprufe LowE SHGC Value=0.479; Intruderprufe LowE U Value=5.33; Intruderprufe SHGC Value=0.539; Intruderprufe U Value=6.7; Is Heavy Duty Handle=0 mm  [stored 0 ft]; Is Heavy Duty Mullion=0 mm  [stored 0 ft]; Limit Sash Width Side Max=1200 mm; Limit Sash Width Side Min=315 mm; Max Pane Area=0.46 m²; Sash Height=810 mm; Sash Width Middle=758 mm; Sash Width Sides=758 mm; Standard Interlocker=Yes; Width=2990 mm  [stored 9.80971 ft]; Windload Design=1500 mm  [stored 4.92126 ft]
- 540SW-3009XXXX-2000Pa: Area Middle Sash Glazing=0.46 m²; Area Side Sash Glazing=0.46 m²; Clearvue SHGC Value=0.572; Custom Windload=2000 mm  [stored 6.56168 ft]; Custom Window Height=890 mm  [stored 2.91995 ft]; Custom Window Width=2990 mm  [stored 9.80971 ft]; Energy Advantage SHGC Value=0.514; Energy Advantage U Value=5.43; Heavy Duty Handle=No; Heavy Duty Interlocker=No; Height=890 mm  [stored 2.91995 ft]; Intruderprufe LowE SHGC Value=0.479; Intruderprufe LowE U Value=5.33; Intruderprufe SHGC Value=0.539; Intruderprufe U Value=6.7; Is Heavy Duty Handle=0 mm  [stored 0 ft]; Is Heavy Duty Mullion=0 mm  [stored 0 ft]; Limit Sash Width Side Max=1200 mm; Limit Sash Width Side Min=315 mm; Max Pane Area=0.46 m²; Sash Height=810 mm; Sash Width Middle=758 mm; Sash Width Sides=758 mm; Standard Interlocker=Yes; Width=2990 mm  [stored 9.80971 ft]; Windload Design=2000 mm  [stored 6.56168 ft]
- 540SW-3012XXXX-1500Pa: Area Middle Sash Glazing=0.65 m²; Area Side Sash Glazing=0.65 m²; Clearvue SHGC Value=0.613; Custom Windload=1500 mm  [stored 4.92126 ft]; Custom Window Height=1190 mm  [stored 3.9042 ft]; Custom Window Width=2990 mm  [stored 9.80971 ft]; Energy Advantage SHGC Value=0.55; Energy Advantage U Value=5.24; Heavy Duty Handle=No; Heavy Duty Interlocker=No; Height=1190 mm  [stored 3.9042 ft]; Intruderprufe LowE SHGC Value=0.513; Intruderprufe LowE U Value=5.15; Intruderprufe SHGC Value=0.578; Intruderprufe U Value=6.62; Is Heavy Duty Handle=0 mm  [stored 0 ft]; Is Heavy Duty Mullion=0 mm  [stored 0 ft]; Limit Sash Width Side Max=1200 mm; Limit Sash Width Side Min=315 mm; Max Pane Area=0.65 m²; Sash Height=1110 mm; Sash Width Middle=758 mm; Sash Width Sides=758 mm; Standard Interlocker=Yes; Width=2990 mm  [stored 9.80971 ft]; Windload Design=1500 mm  [stored 4.92126 ft]
- 540SW-3012XXXX-2000Pa: Area Middle Sash Glazing=0.65 m²; Area Side Sash Glazing=0.65 m²; Clearvue SHGC Value=0.613; Custom Windload=2000 mm  [stored 6.56168 ft]; Custom Window Height=1190 mm  [stored 3.9042 ft]; Custom Window Width=2990 mm  [stored 9.80971 ft]; Energy Advantage SHGC Value=0.55; Energy Advantage U Value=5.24; Heavy Duty Handle=Yes; Heavy Duty Interlocker=Yes; Height=1190 mm  [stored 3.9042 ft]; Intruderprufe LowE SHGC Value=0.513; Intruderprufe LowE U Value=5.15; Intruderprufe SHGC Value=0.578; Intruderprufe U Value=6.62; Is Heavy Duty Handle=1 mm  [stored 0.00328084 ft]; Is Heavy Duty Mullion=1 mm  [stored 0.00328084 ft]; Limit Sash Width Side Max=1200 mm; Limit Sash Width Side Min=315 mm; Max Pane Area=0.65 m²; Sash Height=1110 mm; Sash Width Middle=758 mm; Sash Width Sides=758 mm; Standard Interlocker=No; Width=2990 mm  [stored 9.80971 ft]; Windload Design=2000 mm  [stored 6.56168 ft]
- 540SW-3015XXXX-1500Pa: Area Middle Sash Glazing=0.85 m²; Area Side Sash Glazing=0.85 m²; Clearvue SHGC Value=0.637; Custom Windload=1500 mm  [stored 4.92126 ft]; Custom Window Height=1490 mm  [stored 4.88845 ft]; Custom Window Width=2990 mm  [stored 9.80971 ft]; Energy Advantage SHGC Value=0.572; Energy Advantage U Value=5.13; Heavy Duty Handle=Yes; Heavy Duty Interlocker=Yes; Height=1490 mm  [stored 4.88845 ft]; Intruderprufe LowE SHGC Value=0.533; Intruderprufe LowE U Value=5.04; Intruderprufe SHGC Value=0.601; Intruderprufe U Value=6.58; Is Heavy Duty Handle=1 mm  [stored 0.00328084 ft]; Is Heavy Duty Mullion=1 mm  [stored 0.00328084 ft]; Limit Sash Width Side Max=1200 mm; Limit Sash Width Side Min=315 mm; Max Pane Area=0.85 m²; Sash Height=1410 mm; Sash Width Middle=758 mm; Sash Width Sides=758 mm; Standard Interlocker=No; Width=2990 mm  [stored 9.80971 ft]; Windload Design=1500 mm  [stored 4.92126 ft]
- 540SW-3015XXXX-2000Pa: Area Middle Sash Glazing=0.85 m²; Area Side Sash Glazing=0.85 m²; Clearvue SHGC Value=0.637; Custom Windload=2000 mm  [stored 6.56168 ft]; Custom Window Height=1490 mm  [stored 4.88845 ft]; Custom Window Width=2990 mm  [stored 9.80971 ft]; Energy Advantage SHGC Value=0.572; Energy Advantage U Value=5.13; Heavy Duty Handle=Yes; Heavy Duty Interlocker=Yes; Height=1490 mm  [stored 4.88845 ft]; Intruderprufe LowE SHGC Value=0.533; Intruderprufe LowE U Value=5.04; Intruderprufe SHGC Value=0.601; Intruderprufe U Value=6.58; Is Heavy Duty Handle=1 mm  [stored 0.00328084 ft]; Is Heavy Duty Mullion=1 mm  [stored 0.00328084 ft]; Limit Sash Width Side Max=1200 mm; Limit Sash Width Side Min=315 mm; Max Pane Area=0.85 m²; Sash Height=1410 mm; Sash Width Middle=758 mm; Sash Width Sides=758 mm; Standard Interlocker=No; Width=2990 mm  [stored 9.80971 ft]; Windload Design=2000 mm  [stored 6.56168 ft]

note: [stored X ft] marks values corroborated as IEEE doubles in the binary element streams (Revit-internal decimal feet)

## geometry (parser evidence)
native form markers: Sweep x14
no freeform markers — native parametric forms only
